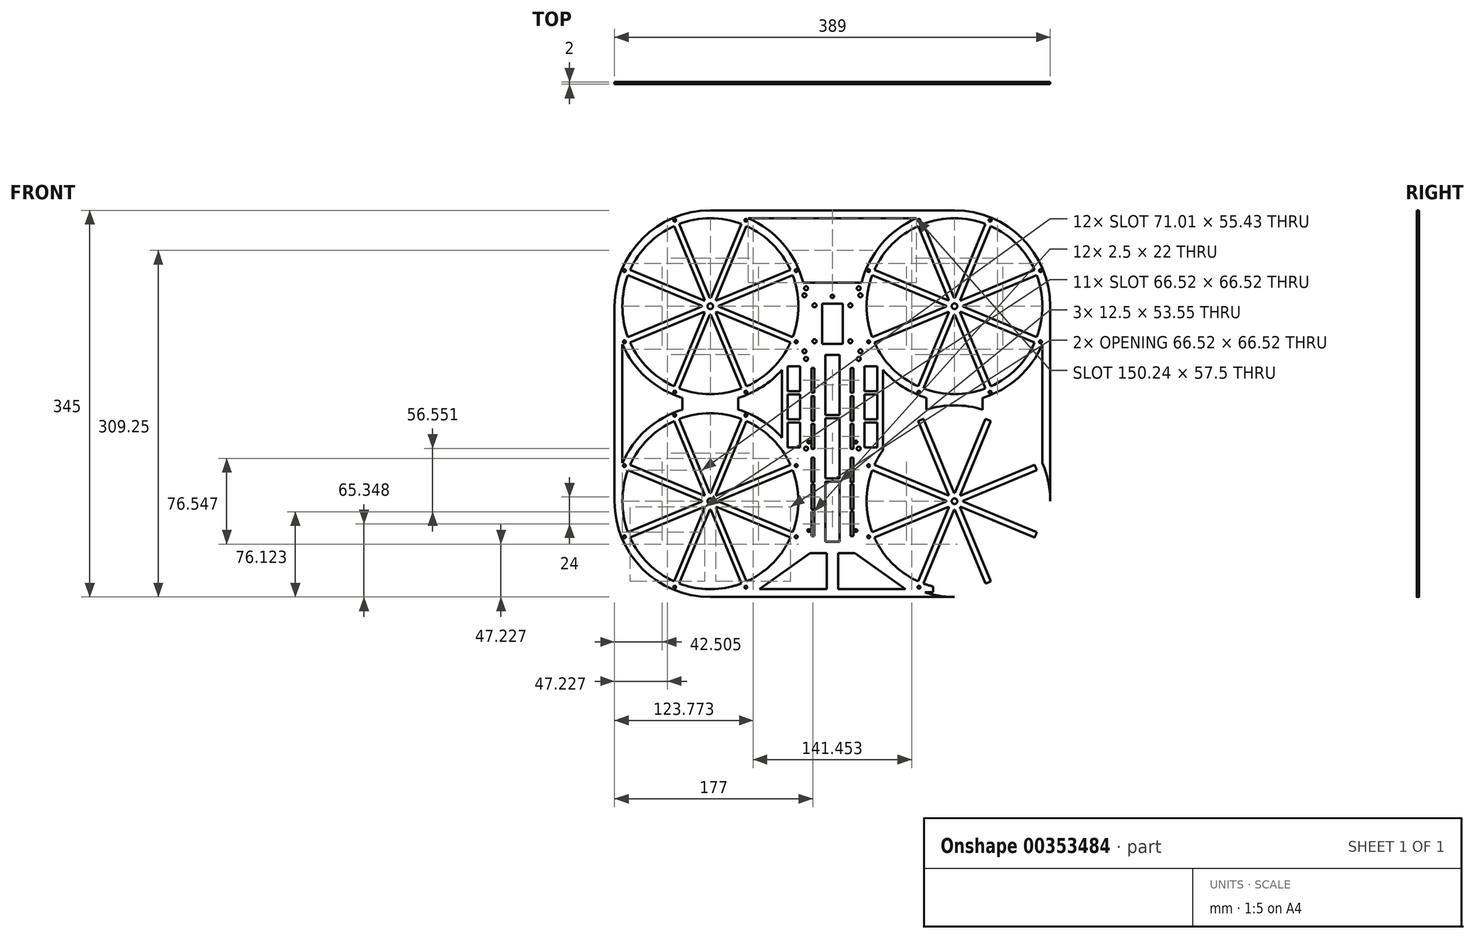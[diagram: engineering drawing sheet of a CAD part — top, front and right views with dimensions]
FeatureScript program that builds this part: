
annotation { "Feature Type Name" : "Feature", "Feature Type Description" : "" }
export const myFeature = defineFeature(function(context is Context, id is Id, definition is map)
    precondition{}
    {
        {
            var Q0;
            Q0=qCreatedBy(makeId("Front.planeOp"),FACE);
            var sketch = newSketch(context, id + "F0", { "sketchPlane" : qUnion([Q0])});
            skLineSegment(sketch, "E0", {"start": v(-45, -241.15) * mm, "end": v(-45, 0) * mm, "construction": true});
            skLineSegment(sketch, "E1", {"start": v(-45, 0) * mm, "end": v(45, 0) * mm});
            skLineSegment(sketch, "E2", {"start": v(45, 0) * mm, "end": v(45, -241.15) * mm, "construction": true});
            skLineSegment(sketch, "E3", {"start": v(5, -241.15) * mm, "end": v(5, -273.5) * mm, "construction": true});
            skLineSegment(sketch, "E4", {"start": v(-5, -273.5) * mm, "end": v(-5, -241.15) * mm, "construction": true});
            skLineSegment(sketch, "E5", {"start": v(-90, -271.29) * mm, "end": v(-90, -276.29) * mm});
            skLineSegment(sketch, "E6", {"start": v(-90, -276.29) * mm, "end": v(90, -276.29) * mm});
            skLineSegment(sketch, "E7", {"start": v(90, -276.29) * mm, "end": v(90, -271.29) * mm});
            skLineSegment(sketch, "E8", {"start": v(45, 0) * mm, "end": v(45, -241.15) * mm});
            skLineSegment(sketch, "E9", {"start": v(-45, 0) * mm, "end": v(-45, -241.15) * mm});
            skLineSegment(sketch, "E10", {"start": v(5, -241.15) * mm, "end": v(5, -273.5) * mm});
            skLineSegment(sketch, "E11", {"start": v(-5, -241.15) * mm, "end": v(-5, -273.5) * mm});
            skCircle(sketch, "E12", {"center": v(21, -221.15) * mm, "radius": 1.25 * mm});
            skCircle(sketch, "E13", {"center": v(21, -142.15) * mm, "radius": 1.25 * mm});
            skLineSegment(sketch, "E14", {"start": v(21, -221.15) * mm, "end": v(21, -142.15) * mm, "construction": true});
            skCircle(sketch, "E15.MirrorC", {"center": v(-21, -142.15) * mm, "radius": 1.25 * mm});
            skCircle(sketch, "E16.MirrorC", {"center": v(-21, -221.15) * mm, "radius": 1.25 * mm});
            skLineSegment(sketch, "E17", {"start": v(-21, -142.15) * mm, "end": v(21, -142.15) * mm});
            skLineSegment(sketch, "E18", {"start": v(-21, -221.15) * mm, "end": v(21, -221.15) * mm});
            skLineSegment(sketch, "E19", {"start": v(-20, -241.15) * mm, "end": v(-5, -241.15) * mm});
            skLineSegment(sketch, "E20", {"start": v(5, -241.15) * mm, "end": v(20, -241.15) * mm});
            skLineSegment(sketch, "E21", {"start": v(-65, -273.5) * mm, "end": v(-5, -273.5) * mm});
            skLineSegment(sketch, "E22", {"start": v(5, -273.5) * mm, "end": v(65, -273.5) * mm});
            skCircle(sketch, "E23", {"center": v(-23.5, -148) * mm, "radius": 1.75 * mm});
            skLineSegment(sketch, "E24", {"start": v(-23.5, -148) * mm, "end": v(-23.5, -5) * mm, "construction": true});
            skLineSegment(sketch, "E25", {"start": v(-23.5, -5) * mm, "end": v(23.5, -5) * mm, "construction": true});
            skCircle(sketch, "E26", {"center": v(-23.5, -5) * mm, "radius": 1.75 * mm});
            skCircle(sketch, "E27", {"center": v(-23.5, -68) * mm, "radius": 1.75 * mm});
            skCircle(sketch, "E28.MirrorC", {"center": v(23.5, -5) * mm, "radius": 1.75 * mm});
            skCircle(sketch, "E29.MirrorC", {"center": v(23.5, -68) * mm, "radius": 1.75 * mm});
            skCircle(sketch, "E30.MirrorC", {"center": v(23.5, -148) * mm, "radius": 1.75 * mm});
            skLineSegment(sketch, "E31.bottom", {"start": v(-108.5, -21) * mm, "end": v(108.5, -21) * mm, "construction": true});
            skLineSegment(sketch, "E31.top", {"start": v(-108.5, -195) * mm, "end": v(108.5, -195) * mm, "construction": true});
            skLineSegment(sketch, "E31.left", {"start": v(-108.5, -21) * mm, "end": v(-108.5, -195) * mm, "construction": true});
            skLineSegment(sketch, "E31.right", {"start": v(108.5, -21) * mm, "end": v(108.5, -195) * mm, "construction": true});
            skCircle(sketch, "E32", {"center": v(-108.5, -21) * mm, "radius": 78.5 * mm, "construction": true});
            skCircle(sketch, "E33", {"center": v(-108.5, -195) * mm, "radius": 78.5 * mm, "construction": true});
            skLineSegment(sketch, "E34", {"start": v(-20, -241.15) * mm, "end": v(-65, -273.5) * mm});
            skLineSegment(sketch, "E35", {"start": v(20, -241.15) * mm, "end": v(65, -273.5) * mm});
            skLineSegment(sketch, "E36", {"start": v(-45, -241.15) * mm, "end": v(-90, -271.29) * mm});
            skLineSegment(sketch, "E37", {"start": v(45, -241.15) * mm, "end": v(90, -271.29) * mm});
            skSolve(sketch);
        }
        {
            var Q0;
            Q0 = qSketchRegion(id + "F0", true);
            var Q1;
            {var subQ0=sQuery(id+"F0.wireOp",EDGE,"kQ9V0P2R-odBh-0fbW-jLHG-dfZg1nlExtGw");Q1=makeQuery(id+"F0.imprint","IMPRINT",FACE,{"disambiguationData":[TD([[makeQuery(id+"F0.imprint","IMPRINT",EDGE,{"derivedFrom":subQ0}),1.0]])]});}
            var Q2;
            {var subQ0=sQuery(id+"F0.wireOp",EDGE,"laIMQzsn-eaY8-GkRH-EcXH-4FRcY363x80o");Q2=makeQuery(id+"F0.imprint","IMPRINT",FACE,{"disambiguationData":[TD([[makeQuery(id+"F0.imprint","IMPRINT",EDGE,{"derivedFrom":subQ0}),-1.0]])]});}
            extrude(context, id + "F1", {"entities" : qUnion([Q0, Q1, Q2]), "offsetDistance" : 25 * mm, "depth" : 2 * mm});
        }
        {
            var Q0;
            Q0=makeQuery(id+"F1.opExtrude","CAP_FACE",FACE,{"disambiguationData":[OSD([sQuery(id+"F0.wireOp",EDGE,"E1"),sQuery(id+"F0.wireOp",EDGE,"E5"),sQuery(id+"F0.wireOp",EDGE,"E6"),sQuery(id+"F0.wireOp",EDGE,"E7"),sQuery(id+"F0.wireOp",EDGE,"E8"),sQuery(id+"F0.wireOp",EDGE,"E9"),sQuery(id+"F0.wireOp",EDGE,"E10"),sQuery(id+"F0.wireOp",EDGE,"E11"),sQuery(id+"F0.wireOp",EDGE,"E12"),sQuery(id+"F0.wireOp",EDGE,"E13"),sQuery(id+"F0.wireOp",EDGE,"E15.MirrorC"),sQuery(id+"F0.wireOp",EDGE,"E16.MirrorC"),sQuery(id+"F0.wireOp",EDGE,"zSTIlZa9-Mq1S-ZDe6-0sfO-W4MshlmDUBfW"),sQuery(id+"F0.wireOp",EDGE,"f6MW2Cg1-CikI-ga4A-lBPH-CLR3HkkBFIXh"),sQuery(id+"F0.wireOp",EDGE,"kKZFOv5i-oTwk-hDfM-zO1L-UuxxMlOX5rbl"),sQuery(id+"F0.wireOp",EDGE,"E19"),sQuery(id+"F0.wireOp",EDGE,"E20"),sQuery(id+"F0.wireOp",EDGE,"xO7viZK4-cgUC-NwoS-h9VV-xVzhR5ju8UwD"),sQuery(id+"F0.wireOp",EDGE,"9yqSDyW4-68Jc-LwH6-pWp7-TDNYJFoeOr4c"),sQuery(id+"F0.wireOp",EDGE,"E21"),sQuery(id+"F0.wireOp",EDGE,"E22"),sQuery(id+"F0.wireOp",EDGE,"pjrDvot8-T0ec-Pg6X-LkKo-KdkXjCvTm1g7"),sQuery(id+"F0.wireOp",EDGE,"E27"),sQuery(id+"F0.wireOp",EDGE,"E26"),sQuery(id+"F0.wireOp",EDGE,"E23"),sQuery(id+"F0.wireOp",EDGE,"E28.MirrorC"),sQuery(id+"F0.wireOp",EDGE,"E29.MirrorC"),sQuery(id+"F0.wireOp",EDGE,"E30.MirrorC"),sQuery(id+"F0.wireOp",EDGE,"6ebM2wVS-usP3-dKcT-XCbS-uj4wceOAEASt"),sQuery(id+"F0.wireOp",EDGE,"DVKAaTnB-kupf-vHmJ-fFrQ-rCFSXDP9MDJ3"),sQuery(id+"F0.wireOp",EDGE,"ROZdGaIm-NAGT-RCMa-KwZE-6l2WkTAMRBSw"),sQuery(id+"F0.wireOp",EDGE,"KL1P7Ti3-s2wI-81Sg-b8aw-ZE9qtUD7GHlb"),sQuery(id+"F0.wireOp",EDGE,"4kzRNWXD-2blB-KAq6-mfhZ-RD1CBBT0MYrh"),sQuery(id+"F0.wireOp",EDGE,"kIW8MdST-1OlK-D9hB-JnCF-jEkgTQVhUQcU"),sQuery(id+"F0.wireOp",EDGE,"r3YkkV02-pVVq-A2jz-rsv9-r8poLlV2KnUy"),sQuery(id+"F0.wireOp",EDGE,"ndt6MnIN-VhPU-kZhu-FrSA-9Hc000Z1pvMu"),sQuery(id+"F0.wireOp",EDGE,"kQ9V0P2R-odBh-0fbW-jLHG-dfZg1nlExtGw"),sQuery(id+"F0.wireOp",EDGE,"Powg7S7J-LFn7-6n4N-oK7u-LEDXEPLRkYPl"),sQuery(id+"F0.wireOp",EDGE,"laIMQzsn-eaY8-GkRH-EcXH-4FRcY363x80o"),sQuery(id+"F0.wireOp",EDGE,"faN3bw6d-osQ8-oTa0-kMRC-kvDlMTcLNJuj")])],"isStart":false});
            var sketch = newSketch(context, id + "F2", { "sketchPlane" : qUnion([Q0])});
            skLineSegment(sketch, "E38.bottom", {"start": v(-25, -11.25) * mm, "end": v(25, -11.25) * mm, "construction": true});
            skLineSegment(sketch, "E38.top", {"start": v(-25, -61.25) * mm, "end": v(25, -61.25) * mm, "construction": true});
            skLineSegment(sketch, "E38.left", {"start": v(-25, -11.25) * mm, "end": v(-25, -61.25) * mm, "construction": true});
            skLineSegment(sketch, "E38.right", {"start": v(25, -11.25) * mm, "end": v(25, -61.25) * mm, "construction": true});
            skCircle(sketch, "E39", {"center": v(-25, -11.25) * mm, "radius": 1.75 * mm});
            skCircle(sketch, "E40", {"center": v(25, -11.25) * mm, "radius": 1.75 * mm});
            skCircle(sketch, "E41", {"center": v(25, -61.25) * mm, "radius": 1.75 * mm});
            skCircle(sketch, "E42", {"center": v(-25, -61.25) * mm, "radius": 1.75 * mm});
            skLineSegment(sketch, "E43.bottom", {"start": v(-17.5, -66.25) * mm, "end": v(17.5, -66.25) * mm, "construction": true});
            skLineSegment(sketch, "E43.top", {"start": v(-17.5, -176.25) * mm, "end": v(17.5, -176.25) * mm, "construction": true});
            skLineSegment(sketch, "E43.left", {"start": v(-17.5, -66.25) * mm, "end": v(-17.5, -176.25) * mm, "construction": true});
            skLineSegment(sketch, "E43.right", {"start": v(17.5, -66.25) * mm, "end": v(17.5, -176.25) * mm, "construction": true});
            skLineSegment(sketch, "E44.bottom", {"start": v(-18.75, -180.15) * mm, "end": v(-16.25, -180.15) * mm});
            skLineSegment(sketch, "E44.top", {"start": v(-18.75, -202.15) * mm, "end": v(-16.25, -202.15) * mm});
            skLineSegment(sketch, "E44.left", {"start": v(-18.75, -180.15) * mm, "end": v(-18.75, -202.15) * mm});
            skLineSegment(sketch, "E44.right", {"start": v(-16.25, -180.15) * mm, "end": v(-16.25, -202.15) * mm});
            skLineSegment(sketch, "E45.bottom", {"start": v(-18.75, -126.15) * mm, "end": v(-16.25, -126.15) * mm});
            skLineSegment(sketch, "E45.top", {"start": v(-18.75, -148.15) * mm, "end": v(-16.25, -148.15) * mm});
            skLineSegment(sketch, "E45.left", {"start": v(-18.75, -126.15) * mm, "end": v(-18.75, -148.15) * mm});
            skLineSegment(sketch, "E45.right", {"start": v(-16.25, -126.15) * mm, "end": v(-16.25, -148.15) * mm});
            skLineSegment(sketch, "E46.bottom", {"start": v(-18.75, -204.15) * mm, "end": v(-16.25, -204.15) * mm});
            skLineSegment(sketch, "E46.top", {"start": v(-18.75, -226.15) * mm, "end": v(-16.25, -226.15) * mm});
            skLineSegment(sketch, "E46.left", {"start": v(-18.75, -204.15) * mm, "end": v(-18.75, -226.15) * mm});
            skLineSegment(sketch, "E46.right", {"start": v(-16.25, -204.15) * mm, "end": v(-16.25, -226.15) * mm});
            skLineSegment(sketch, "E47.bottom", {"start": v(-18.75, -156.15) * mm, "end": v(-16.25, -156.15) * mm});
            skLineSegment(sketch, "E47.top", {"start": v(-18.75, -178.15) * mm, "end": v(-16.25, -178.15) * mm});
            skLineSegment(sketch, "E47.left", {"start": v(-18.75, -156.15) * mm, "end": v(-18.75, -178.15) * mm});
            skLineSegment(sketch, "E47.right", {"start": v(-16.25, -156.15) * mm, "end": v(-16.25, -178.15) * mm});
            skLineSegment(sketch, "E48.MirrorCS", {"start": v(18.75, -180.15) * mm, "end": v(16.25, -180.15) * mm});
            skLineSegment(sketch, "E49.MirrorCS", {"start": v(17.5, -66.25) * mm, "end": v(-17.5, -66.25) * mm, "construction": true});
            skLineSegment(sketch, "E50.MirrorCS", {"start": v(18.75, -126.15) * mm, "end": v(16.25, -126.15) * mm});
            skLineSegment(sketch, "E51.MirrorCS", {"start": v(18.75, -148.15) * mm, "end": v(16.25, -148.15) * mm});
            skLineSegment(sketch, "E52.MirrorCS", {"start": v(18.75, -202.15) * mm, "end": v(16.25, -202.15) * mm});
            skLineSegment(sketch, "E53.MirrorCS", {"start": v(18.75, -204.15) * mm, "end": v(16.25, -204.15) * mm});
            skLineSegment(sketch, "E54.MirrorCS", {"start": v(18.75, -156.15) * mm, "end": v(16.25, -156.15) * mm});
            skLineSegment(sketch, "E55.MirrorCS", {"start": v(18.75, -226.15) * mm, "end": v(16.25, -226.15) * mm});
            skLineSegment(sketch, "E56.MirrorCS", {"start": v(18.75, -178.15) * mm, "end": v(16.25, -178.15) * mm});
            skLineSegment(sketch, "E57.MirrorCS", {"start": v(18.75, -204.15) * mm, "end": v(18.75, -226.15) * mm});
            skLineSegment(sketch, "E58.MirrorCS", {"start": v(18.75, -126.15) * mm, "end": v(18.75, -148.15) * mm});
            skLineSegment(sketch, "E59.MirrorCS", {"start": v(16.25, -126.15) * mm, "end": v(16.25, -148.15) * mm});
            skLineSegment(sketch, "E60.MirrorCS", {"start": v(18.75, -156.15) * mm, "end": v(18.75, -178.15) * mm});
            skLineSegment(sketch, "E61.MirrorCS", {"start": v(16.25, -204.15) * mm, "end": v(16.25, -226.15) * mm});
            skLineSegment(sketch, "E62.MirrorCS", {"start": v(16.25, -180.15) * mm, "end": v(16.25, -202.15) * mm});
            skLineSegment(sketch, "E63.MirrorCS", {"start": v(18.75, -180.15) * mm, "end": v(18.75, -202.15) * mm});
            skLineSegment(sketch, "E64.MirrorCS", {"start": v(16.25, -156.15) * mm, "end": v(16.25, -178.15) * mm});
            skCircle(sketch, "E65", {"center": v(-25, -11.25) * mm, "radius": 2.75 * mm, "construction": true});
            skCircle(sketch, "E66", {"center": v(-23.5, -5) * mm, "radius": 2.75 * mm, "construction": true});
            skLineSegment(sketch, "E67.bottom", {"start": v(-16, -20.25) * mm, "end": v(16, -20.25) * mm, "construction": true});
            skLineSegment(sketch, "E67.top", {"start": v(-16, -52.25) * mm, "end": v(16, -52.25) * mm, "construction": true});
            skLineSegment(sketch, "E67.left", {"start": v(-16, -20.25) * mm, "end": v(-16, -52.25) * mm, "construction": true});
            skLineSegment(sketch, "E67.right", {"start": v(16, -20.25) * mm, "end": v(16, -52.25) * mm, "construction": true});
            skCircle(sketch, "E68", {"center": v(16, -20.25) * mm, "radius": 1.75 * mm});
            skCircle(sketch, "E69", {"center": v(16, -52.25) * mm, "radius": 1.75 * mm});
            skCircle(sketch, "E70", {"center": v(-16, -52.25) * mm, "radius": 1.75 * mm});
            skCircle(sketch, "E71", {"center": v(-16, -20.25) * mm, "radius": 1.75 * mm});
            skLineSegment(sketch, "E72.0.1.0", {"start": v(16.25, -101.15) * mm, "end": v(16.25, -123.15) * mm});
            skLineSegment(sketch, "E72.0.1.1", {"start": v(-18.75, -101.15) * mm, "end": v(-18.75, -123.15) * mm});
            skLineSegment(sketch, "E72.0.1.2", {"start": v(-16.25, -101.15) * mm, "end": v(-16.25, -123.15) * mm});
            skLineSegment(sketch, "E72.0.1.3", {"start": v(18.75, -101.15) * mm, "end": v(18.75, -123.15) * mm});
            skLineSegment(sketch, "E72.0.1.4", {"start": v(-18.75, -123.15) * mm, "end": v(-16.25, -123.15) * mm});
            skLineSegment(sketch, "E72.0.1.5", {"start": v(18.75, -123.15) * mm, "end": v(16.25, -123.15) * mm});
            skLineSegment(sketch, "E72.0.1.6", {"start": v(-18.75, -101.15) * mm, "end": v(-16.25, -101.15) * mm});
            skLineSegment(sketch, "E72.0.1.7", {"start": v(18.75, -101.15) * mm, "end": v(16.25, -101.15) * mm});
            skLineSegment(sketch, "E72.0.2.0", {"start": v(16.25, -76.15) * mm, "end": v(16.25, -98.15) * mm});
            skLineSegment(sketch, "E72.0.2.1", {"start": v(-18.75, -76.15) * mm, "end": v(-18.75, -98.15) * mm});
            skLineSegment(sketch, "E72.0.2.2", {"start": v(-16.25, -76.15) * mm, "end": v(-16.25, -98.15) * mm});
            skLineSegment(sketch, "E72.0.2.3", {"start": v(18.75, -76.15) * mm, "end": v(18.75, -98.15) * mm});
            skLineSegment(sketch, "E72.0.2.4", {"start": v(-18.75, -98.15) * mm, "end": v(-16.25, -98.15) * mm});
            skLineSegment(sketch, "E72.0.2.5", {"start": v(18.75, -98.15) * mm, "end": v(16.25, -98.15) * mm});
            skLineSegment(sketch, "E72.0.2.6", {"start": v(-18.75, -76.15) * mm, "end": v(-16.25, -76.15) * mm});
            skLineSegment(sketch, "E72.0.2.7", {"start": v(18.75, -76.15) * mm, "end": v(16.25, -76.15) * mm});
            skLineSegment(sketch, "E72.direction1", {"start": v(-18.75, -148.15) * mm, "end": v(6.25, -148.15) * mm, "construction": true});
            skLineSegment(sketch, "E72.direction2", {"start": v(-18.75, -148.15) * mm, "end": v(-18.75, -123.15) * mm, "construction": true});
            skSolve(sketch);
        }
        {
            var Q0;
            Q0 = qSketchRegion(id + "F2", true);
            extrude(context, id + "F3", {"entities" : qUnion([Q0]), "operationType" : NewBodyOperationType.REMOVE, "endBound" : BoundingType.THROUGH_ALL, "oppositeDirection" : true, "depth" : 25 * mm, "offsetDistance" : 25 * mm});
        }
        {
            var Q0;
            Q0=makeQuery(id+"F1.opExtrude","CAP_FACE",FACE,{"disambiguationData":[OSD([sQuery(id+"F0.wireOp",EDGE,"E1"),sQuery(id+"F0.wireOp",EDGE,"E5"),sQuery(id+"F0.wireOp",EDGE,"E6"),sQuery(id+"F0.wireOp",EDGE,"E7"),sQuery(id+"F0.wireOp",EDGE,"E8"),sQuery(id+"F0.wireOp",EDGE,"E9"),sQuery(id+"F0.wireOp",EDGE,"E10"),sQuery(id+"F0.wireOp",EDGE,"E11"),sQuery(id+"F0.wireOp",EDGE,"E12"),sQuery(id+"F0.wireOp",EDGE,"E13"),sQuery(id+"F0.wireOp",EDGE,"E15.MirrorC"),sQuery(id+"F0.wireOp",EDGE,"E16.MirrorC"),sQuery(id+"F0.wireOp",EDGE,"zSTIlZa9-Mq1S-ZDe6-0sfO-W4MshlmDUBfW"),sQuery(id+"F0.wireOp",EDGE,"f6MW2Cg1-CikI-ga4A-lBPH-CLR3HkkBFIXh"),sQuery(id+"F0.wireOp",EDGE,"kKZFOv5i-oTwk-hDfM-zO1L-UuxxMlOX5rbl"),sQuery(id+"F0.wireOp",EDGE,"E19"),sQuery(id+"F0.wireOp",EDGE,"E20"),sQuery(id+"F0.wireOp",EDGE,"xO7viZK4-cgUC-NwoS-h9VV-xVzhR5ju8UwD"),sQuery(id+"F0.wireOp",EDGE,"9yqSDyW4-68Jc-LwH6-pWp7-TDNYJFoeOr4c"),sQuery(id+"F0.wireOp",EDGE,"E21"),sQuery(id+"F0.wireOp",EDGE,"E22"),sQuery(id+"F0.wireOp",EDGE,"pjrDvot8-T0ec-Pg6X-LkKo-KdkXjCvTm1g7"),sQuery(id+"F0.wireOp",EDGE,"E27"),sQuery(id+"F0.wireOp",EDGE,"E26"),sQuery(id+"F0.wireOp",EDGE,"E23"),sQuery(id+"F0.wireOp",EDGE,"E28.MirrorC"),sQuery(id+"F0.wireOp",EDGE,"E29.MirrorC"),sQuery(id+"F0.wireOp",EDGE,"E30.MirrorC")])],"isStart":false});
            var sketch = newSketch(context, id + "F4", { "sketchPlane" : qUnion([Q0])});
            skLineSegment(sketch, "E73.bottom", {"start": v(-109, -21) * mm, "end": v(109, -21) * mm, "construction": true});
            skLineSegment(sketch, "E73.top", {"start": v(-109, -195) * mm, "end": v(109, -195) * mm, "construction": true});
            skLineSegment(sketch, "E73.left", {"start": v(-109, -21) * mm, "end": v(-109, -195) * mm, "construction": true});
            skLineSegment(sketch, "E73.right", {"start": v(109, -21) * mm, "end": v(109, -195) * mm, "construction": true});
            skCircle(sketch, "E74", {"center": v(-109, -21) * mm, "radius": 78.5 * mm, "construction": true});
            skCircle(sketch, "E75", {"center": v(109, -21) * mm, "radius": 78.5 * mm, "construction": true});
            skLineSegment(sketch, "E76", {"start": v(-33.36, 0) * mm, "end": v(-45, 0) * mm});
            skLineSegment(sketch, "E77", {"start": v(-45, 0) * mm, "end": v(-45, -66.46) * mm});
            skLineSegment(sketch, "E78", {"start": v(33.36, 0) * mm, "end": v(45, 0) * mm});
            skLineSegment(sketch, "E79", {"start": v(45, 0) * mm, "end": v(45, -66.46) * mm});
            skArc(sketch, "E80", {"start": v(-33.36, 0) * mm, "mid": v(-31.68, -34.54) * mm, "end": v(-45, -66.46) * mm});
            skArc(sketch, "E81", {"start": v(33.36, 0) * mm, "mid": v(31.68, -34.54) * mm, "end": v(45, -66.46) * mm});
            skCircle(sketch, "E82", {"center": v(-109, -21) * mm, "radius": 85.5 * mm, "construction": true});
            skCircle(sketch, "E83", {"center": v(109, -195) * mm, "radius": 78.5 * mm, "construction": true});
            skCircle(sketch, "E84", {"center": v(109, -195) * mm, "radius": 85.5 * mm, "construction": true});
            skCircle(sketch, "E85", {"center": v(-109, -195) * mm, "radius": 78.5 * mm, "construction": true});
            skCircle(sketch, "E86", {"center": v(-109, -195) * mm, "radius": 85.5 * mm, "construction": true});
            skCircle(sketch, "E87", {"center": v(109, -21) * mm, "radius": 85.5 * mm, "construction": true});
            skCircle(sketch, "E88.cCircle", {"center": v(109, -195) * mm, "radius": 83 * mm, "construction": true});
            skLineSegment(sketch, "E88.0", {"start": v(140.76, -118.32) * mm, "end": v(185.68, -163.24) * mm, "construction": true});
            skLineSegment(sketch, "E88.1", {"start": v(185.68, -163.24) * mm, "end": v(185.68, -226.76) * mm, "construction": true});
            skLineSegment(sketch, "E88.2", {"start": v(185.68, -226.76) * mm, "end": v(140.76, -271.68) * mm, "construction": true});
            skLineSegment(sketch, "E88.3", {"start": v(140.76, -271.68) * mm, "end": v(77.24, -271.68) * mm, "construction": true});
            skLineSegment(sketch, "E88.4", {"start": v(77.24, -271.68) * mm, "end": v(32.32, -226.76) * mm, "construction": true});
            skLineSegment(sketch, "E88.5", {"start": v(32.32, -226.76) * mm, "end": v(32.32, -163.24) * mm, "construction": true});
            skLineSegment(sketch, "E88.6", {"start": v(32.32, -163.24) * mm, "end": v(77.24, -118.32) * mm, "construction": true});
            skLineSegment(sketch, "E88.7", {"start": v(77.24, -118.32) * mm, "end": v(140.76, -118.32) * mm, "construction": true});
            skCircle(sketch, "E89.cCircle", {"center": v(-109, -21) * mm, "radius": 83 * mm, "construction": true});
            skLineSegment(sketch, "E89.0", {"start": v(-185.68, 10.76) * mm, "end": v(-140.76, 55.68) * mm, "construction": true});
            skLineSegment(sketch, "E89.1", {"start": v(-140.76, 55.68) * mm, "end": v(-77.24, 55.68) * mm, "construction": true});
            skLineSegment(sketch, "E89.2", {"start": v(-77.24, 55.68) * mm, "end": v(-32.32, 10.76) * mm, "construction": true});
            skLineSegment(sketch, "E89.3", {"start": v(-32.32, 10.76) * mm, "end": v(-32.32, -52.76) * mm, "construction": true});
            skLineSegment(sketch, "E89.4", {"start": v(-32.32, -52.76) * mm, "end": v(-77.24, -97.68) * mm, "construction": true});
            skLineSegment(sketch, "E89.5", {"start": v(-77.24, -97.68) * mm, "end": v(-140.76, -97.68) * mm, "construction": true});
            skLineSegment(sketch, "E89.6", {"start": v(-140.76, -97.68) * mm, "end": v(-185.68, -52.76) * mm, "construction": true});
            skLineSegment(sketch, "E89.7", {"start": v(-185.68, -52.76) * mm, "end": v(-185.68, 10.76) * mm, "construction": true});
            skCircle(sketch, "E90.cCircle", {"center": v(109, -21) * mm, "radius": 83 * mm, "construction": true});
            skLineSegment(sketch, "E90.0", {"start": v(140.76, 55.68) * mm, "end": v(185.68, 10.76) * mm, "construction": true});
            skLineSegment(sketch, "E90.1", {"start": v(185.68, 10.76) * mm, "end": v(185.68, -52.76) * mm, "construction": true});
            skLineSegment(sketch, "E90.2", {"start": v(185.68, -52.76) * mm, "end": v(140.76, -97.68) * mm, "construction": true});
            skLineSegment(sketch, "E90.3", {"start": v(140.76, -97.68) * mm, "end": v(77.24, -97.68) * mm, "construction": true});
            skLineSegment(sketch, "E90.4", {"start": v(77.24, -97.68) * mm, "end": v(32.32, -52.76) * mm, "construction": true});
            skLineSegment(sketch, "E90.5", {"start": v(32.32, -52.76) * mm, "end": v(32.32, 10.76) * mm, "construction": true});
            skLineSegment(sketch, "E90.6", {"start": v(32.32, 10.76) * mm, "end": v(77.24, 55.68) * mm, "construction": true});
            skLineSegment(sketch, "E90.7", {"start": v(77.24, 55.68) * mm, "end": v(140.76, 55.68) * mm, "construction": true});
            skCircle(sketch, "E91.cCircle", {"center": v(-109, -195) * mm, "radius": 83 * mm, "construction": true});
            skLineSegment(sketch, "E91.0", {"start": v(-140.76, -118.32) * mm, "end": v(-77.24, -118.32) * mm, "construction": true});
            skLineSegment(sketch, "E91.1", {"start": v(-77.24, -118.32) * mm, "end": v(-32.32, -163.24) * mm, "construction": true});
            skLineSegment(sketch, "E91.2", {"start": v(-32.32, -163.24) * mm, "end": v(-32.32, -226.76) * mm, "construction": true});
            skLineSegment(sketch, "E91.3", {"start": v(-32.32, -226.76) * mm, "end": v(-77.24, -271.68) * mm, "construction": true});
            skLineSegment(sketch, "E91.4", {"start": v(-77.24, -271.68) * mm, "end": v(-140.76, -271.68) * mm, "construction": true});
            skLineSegment(sketch, "E91.5", {"start": v(-140.76, -271.68) * mm, "end": v(-185.68, -226.76) * mm, "construction": true});
            skLineSegment(sketch, "E91.6", {"start": v(-185.68, -226.76) * mm, "end": v(-185.68, -163.24) * mm, "construction": true});
            skLineSegment(sketch, "E91.7", {"start": v(-185.68, -163.24) * mm, "end": v(-140.76, -118.32) * mm, "construction": true});
            skCircle(sketch, "E92", {"center": v(-32.32, -52.76) * mm, "radius": 1.25 * mm});
            skCircle(sketch, "E93", {"center": v(-32.32, -163.24) * mm, "radius": 1.25 * mm});
            skCircle(sketch, "E94", {"center": v(32.32, -163.24) * mm, "radius": 1.25 * mm});
            skCircle(sketch, "E95", {"center": v(32.32, -52.76) * mm, "radius": 1.25 * mm});
            skCircle(sketch, "E96", {"center": v(-140.76, -118.32) * mm, "radius": 1.25 * mm, "construction": true});
            skCircle(sketch, "E97", {"center": v(-25, -11.25) * mm, "radius": 3 * mm, "construction": true});
            skCircle(sketch, "E98", {"center": v(-23.5, -5) * mm, "radius": 3 * mm, "construction": true});
            skLineSegment(sketch, "E99", {"start": v(-26.12, 0) * mm, "end": v(-28.5, 0) * mm, "construction": true});
            skLineSegment(sketch, "E100", {"start": v(-28.5, 0) * mm, "end": v(-28.5, -42) * mm, "construction": true});
            skLineSegment(sketch, "E101", {"start": v(-28.5, -42) * mm, "end": v(-26.12, -42) * mm, "construction": true});
            skLineSegment(sketch, "E102", {"start": v(-109, -116.5) * mm, "end": v(-190.8, -116.5) * mm, "construction": true});
            skLineSegment(sketch, "E103", {"start": v(0, -195) * mm, "end": v(-32.32, -226.76) * mm, "construction": true});
            skLineSegment(sketch, "E104", {"start": v(32.32, -226.76) * mm, "end": v(-32.32, -226.76) * mm, "construction": true});
            skLineSegment(sketch, "E105", {"start": v(32.32, -226.76) * mm, "end": v(0, -195) * mm, "construction": true});
            skLineSegment(sketch, "E106", {"start": v(0, -203.76) * mm, "end": v(0, -226.76) * mm, "construction": true});
            skPoint(sketch, "E106.endSnap0", {"position": v(0, -226.76) * mm});
            skLineSegment(sketch, "E107", {"start": v(-32.32, 10.76) * mm, "end": v(32.32, 10.76) * mm, "construction": true});
            skLineSegment(sketch, "E108", {"start": v(32.32, 10.76) * mm, "end": v(0, -12.24) * mm, "construction": true});
            skLineSegment(sketch, "E109", {"start": v(0, -12.24) * mm, "end": v(-32.32, 10.76) * mm, "construction": true});
            skCircle(sketch, "E110", {"center": v(0, -203.76) * mm, "radius": 1.5 * mm});
            skCircle(sketch, "E111", {"center": v(0, -12.24) * mm, "radius": 1.5 * mm});
            skArc(sketch, "E112", {"start": v(-33.36, 0) * mm, "mid": v(-186.32, -7.46) * mm, "end": v(-45, -66.46) * mm});
            skArc(sketch, "E113", {"start": v(-26.12, 0) * mm, "mid": v(-192.08, -0.8) * mm, "end": v(-45, -77.7) * mm, "construction": true});
            skLineSegment(sketch, "E114", {"start": v(-33.36, 0) * mm, "end": v(-26.12, 0) * mm});
            skLineSegment(sketch, "E115", {"start": v(-45, -77.7) * mm, "end": v(-45, -66.46) * mm});
            skArc(sketch, "E116", {"start": v(-45, -77.7) * mm, "mid": v(-192.08, -0.8) * mm, "end": v(-26.12, 0) * mm});
            skArc(sketch, "E117", {"start": v(45, -66.46) * mm, "mid": v(186.32, -7.46) * mm, "end": v(33.36, 0) * mm});
            skArc(sketch, "E118", {"start": v(26.12, 0) * mm, "mid": v(192.08, -0.8) * mm, "end": v(45, -77.7) * mm});
            skArc(sketch, "E119", {"start": v(-45, -149.54) * mm, "mid": v(-35.38, -222.24) * mm, "end": v(-90, -271.17) * mm});
            skLineSegment(sketch, "E120", {"start": v(-45, -149.54) * mm, "end": v(-45, -241.15) * mm});
            skLineSegment(sketch, "E121", {"start": v(-45, -241.15) * mm, "end": v(-90, -271.29) * mm});
            skLineSegment(sketch, "E122", {"start": v(-90, -271.29) * mm, "end": v(-90, -271.29) * mm});
            skLineSegment(sketch, "E123", {"start": v(-90, -271.17) * mm, "end": v(-90, -271.29) * mm});
            skArc(sketch, "E124", {"start": v(-45, -138.3) * mm, "mid": v(-191.5, -172.58) * mm, "end": v(-82.5, -276.29) * mm});
            skArc(sketch, "E125", {"start": v(-45, -149.54) * mm, "mid": v(-182.62, -167.76) * mm, "end": v(-90, -271.17) * mm});
            skLineSegment(sketch, "E126.MirrorCS", {"start": v(45, -149.54) * mm, "end": v(45, -241.15) * mm});
            skLineSegment(sketch, "E127.MirrorCS", {"start": v(-32.32, -226.76) * mm, "end": v(32.32, -226.76) * mm, "construction": true});
            skLineSegment(sketch, "E128.MirrorCS", {"start": v(32.32, -226.76) * mm, "end": v(77.24, -271.68) * mm, "construction": true});
            skLineSegment(sketch, "E129.MirrorCS", {"start": v(32.32, -163.24) * mm, "end": v(32.32, -226.76) * mm, "construction": true});
            skArc(sketch, "E130", {"start": v(45, -149.54) * mm, "mid": v(35.38, -222.24) * mm, "end": v(90, -271.17) * mm});
            skLineSegment(sketch, "E131", {"start": v(90, -271.29) * mm, "end": v(90, -271.17) * mm});
            skLineSegment(sketch, "E132", {"start": v(90, -271.29) * mm, "end": v(45, -241.15) * mm});
            skArc(sketch, "E133", {"start": v(45, -138.3) * mm, "mid": v(191.5, -172.58) * mm, "end": v(82.5, -276.29) * mm});
            skArc(sketch, "E134", {"start": v(90, -271.17) * mm, "mid": v(182.62, -167.76) * mm, "end": v(45, -149.54) * mm});
            skSolve(sketch);
        }
        {
            var Q0;
            Q0 = qSketchRegion(id + "F4", true);
            extrude(context, id + "F5", {"entities" : qUnion([Q0]), "operationType" : NewBodyOperationType.REMOVE, "endBound" : BoundingType.THROUGH_ALL, "oppositeDirection" : true, "depth" : 25 * mm, "offsetDistance" : 25 * mm});
        }
        {
            var Q0;
            Q0=makeQuery(id+"FMxjOZTch3q8zvc_1.boolean.opBoolean","MERGE",FACE,{"derivedFrom":[makeQuery(id+"F1.opExtrude","CAP_FACE",FACE,{"disambiguationData":[OSD([sQuery(id+"F0.wireOp",EDGE,"E1"),sQuery(id+"F0.wireOp",EDGE,"E5"),sQuery(id+"F0.wireOp",EDGE,"E6"),sQuery(id+"F0.wireOp",EDGE,"E7"),sQuery(id+"F0.wireOp",EDGE,"E8"),sQuery(id+"F0.wireOp",EDGE,"E9"),sQuery(id+"F0.wireOp",EDGE,"E10"),sQuery(id+"F0.wireOp",EDGE,"E11"),sQuery(id+"F0.wireOp",EDGE,"E12"),sQuery(id+"F0.wireOp",EDGE,"E13"),sQuery(id+"F0.wireOp",EDGE,"E15.MirrorC"),sQuery(id+"F0.wireOp",EDGE,"E16.MirrorC"),sQuery(id+"F0.wireOp",EDGE,"zSTIlZa9-Mq1S-ZDe6-0sfO-W4MshlmDUBfW"),sQuery(id+"F0.wireOp",EDGE,"f6MW2Cg1-CikI-ga4A-lBPH-CLR3HkkBFIXh"),sQuery(id+"F0.wireOp",EDGE,"kKZFOv5i-oTwk-hDfM-zO1L-UuxxMlOX5rbl"),sQuery(id+"F0.wireOp",EDGE,"E19"),sQuery(id+"F0.wireOp",EDGE,"E20"),sQuery(id+"F0.wireOp",EDGE,"xO7viZK4-cgUC-NwoS-h9VV-xVzhR5ju8UwD"),sQuery(id+"F0.wireOp",EDGE,"9yqSDyW4-68Jc-LwH6-pWp7-TDNYJFoeOr4c"),sQuery(id+"F0.wireOp",EDGE,"E21"),sQuery(id+"F0.wireOp",EDGE,"E22"),sQuery(id+"F0.wireOp",EDGE,"pjrDvot8-T0ec-Pg6X-LkKo-KdkXjCvTm1g7"),sQuery(id+"F0.wireOp",EDGE,"E27"),sQuery(id+"F0.wireOp",EDGE,"E26"),sQuery(id+"F0.wireOp",EDGE,"E23"),sQuery(id+"F0.wireOp",EDGE,"E28.MirrorC"),sQuery(id+"F0.wireOp",EDGE,"E29.MirrorC"),sQuery(id+"F0.wireOp",EDGE,"E30.MirrorC")])],"isStart":false})],"fromTools":[makeQuery(id+"FMxjOZTch3q8zvc_1.opExtrude","SWEPT_FACE",FACE,{"disambiguationData":[OSD([sQuery(id+"FXnTs9Vk96qBHkO_1.wireOp",EDGE,"2qYHMhsn-Td8y-HjAB-3SRO-Tm7Y1iTeiUua.top")])]}),makeQuery(id+"FMxjOZTch3q8zvc_1.opExtrude","SWEPT_FACE",FACE,{"disambiguationData":[OSD([sQuery(id+"FXnTs9Vk96qBHkO_1.wireOp",EDGE,"225656be-2882-4732-a1c9-cd1c7ffdf3812.MirrorCS")])]})]});
            var sketch = newSketch(context, id + "F6", { "sketchPlane" : qUnion([Q0])});
            skLineSegment(sketch, "E135.bottom", {"start": v(-40, -74.75) * mm, "end": v(-28.75, -74.75) * mm});
            skLineSegment(sketch, "E135.top", {"start": v(-40, -96.83) * mm, "end": v(-28.75, -96.83) * mm});
            skLineSegment(sketch, "E135.left", {"start": v(-40, -74.75) * mm, "end": v(-40, -96.83) * mm});
            skLineSegment(sketch, "E135.right", {"start": v(-28.75, -74.75) * mm, "end": v(-28.75, -96.83) * mm});
            skLineSegment(sketch, "E136.bottom", {"start": v(28.75, -74.75) * mm, "end": v(40, -74.75) * mm});
            skLineSegment(sketch, "E136.top", {"start": v(28.75, -96.83) * mm, "end": v(40, -96.83) * mm});
            skLineSegment(sketch, "E136.left", {"start": v(28.75, -74.75) * mm, "end": v(28.75, -96.83) * mm});
            skLineSegment(sketch, "E136.right", {"start": v(40, -74.75) * mm, "end": v(40, -96.83) * mm});
            skLineSegment(sketch, "E137.bottom", {"start": v(-6.25, -64.5) * mm, "end": v(6.25, -64.5) * mm});
            skLineSegment(sketch, "E137.top", {"start": v(-6.25, -118.05) * mm, "end": v(6.25, -118.05) * mm});
            skLineSegment(sketch, "E137.left", {"start": v(-6.25, -64.5) * mm, "end": v(-6.25, -118.05) * mm});
            skLineSegment(sketch, "E137.right", {"start": v(6.25, -64.5) * mm, "end": v(6.25, -118.05) * mm});
            skLineSegment(sketch, "E138.bottom", {"start": v(-9.25, -18.74) * mm, "end": v(9.25, -18.74) * mm});
            skLineSegment(sketch, "E138.top", {"start": v(-9.25, -54.5) * mm, "end": v(9.25, -54.5) * mm});
            skLineSegment(sketch, "E138.left", {"start": v(-9.25, -18.74) * mm, "end": v(-9.25, -54.5) * mm});
            skLineSegment(sketch, "E138.right", {"start": v(9.25, -18.74) * mm, "end": v(9.25, -54.5) * mm});
            skLineSegment(sketch, "E139.bottom", {"start": v(-6.25, -177.6) * mm, "end": v(6.25, -177.6) * mm});
            skLineSegment(sketch, "E139.top", {"start": v(-6.25, -231.15) * mm, "end": v(6.25, -231.15) * mm});
            skLineSegment(sketch, "E139.left", {"start": v(-6.25, -177.6) * mm, "end": v(-6.25, -231.15) * mm});
            skLineSegment(sketch, "E139.right", {"start": v(6.25, -177.6) * mm, "end": v(6.25, -231.15) * mm});
            skLineSegment(sketch, "E140.bottom", {"start": v(-6.25, -121.05) * mm, "end": v(6.25, -121.05) * mm});
            skLineSegment(sketch, "E140.top", {"start": v(-6.25, -174.6) * mm, "end": v(6.25, -174.6) * mm});
            skLineSegment(sketch, "E140.left", {"start": v(-6.25, -121.05) * mm, "end": v(-6.25, -174.6) * mm});
            skLineSegment(sketch, "E140.right", {"start": v(6.25, -121.05) * mm, "end": v(6.25, -174.6) * mm});
            skLineSegment(sketch, "E141.bottom", {"start": v(28.75, -99.83) * mm, "end": v(40, -99.83) * mm});
            skLineSegment(sketch, "E141.top", {"start": v(28.75, -121.9) * mm, "end": v(40, -121.9) * mm});
            skLineSegment(sketch, "E141.left", {"start": v(28.75, -99.83) * mm, "end": v(28.75, -121.9) * mm});
            skLineSegment(sketch, "E141.right", {"start": v(40, -99.83) * mm, "end": v(40, -121.9) * mm});
            skLineSegment(sketch, "E142.bottom", {"start": v(28.75, -124.9) * mm, "end": v(40, -124.9) * mm});
            skLineSegment(sketch, "E142.top", {"start": v(28.75, -146.99) * mm, "end": v(40, -146.99) * mm});
            skLineSegment(sketch, "E142.left", {"start": v(28.75, -124.9) * mm, "end": v(28.75, -146.99) * mm});
            skLineSegment(sketch, "E142.right", {"start": v(40, -124.9) * mm, "end": v(40, -146.99) * mm});
            skLineSegment(sketch, "E143.bottom", {"start": v(-40, -99.83) * mm, "end": v(-28.75, -99.83) * mm});
            skLineSegment(sketch, "E143.top", {"start": v(-40, -121.9) * mm, "end": v(-28.75, -121.9) * mm});
            skLineSegment(sketch, "E143.left", {"start": v(-40, -99.83) * mm, "end": v(-40, -121.9) * mm});
            skLineSegment(sketch, "E143.right", {"start": v(-28.75, -99.83) * mm, "end": v(-28.75, -121.9) * mm});
            skLineSegment(sketch, "E144.bottom", {"start": v(-28.75, -124.9) * mm, "end": v(-40, -124.9) * mm});
            skLineSegment(sketch, "E144.top", {"start": v(-28.75, -146.99) * mm, "end": v(-40, -146.99) * mm});
            skLineSegment(sketch, "E144.left", {"start": v(-28.75, -124.9) * mm, "end": v(-28.75, -146.99) * mm});
            skLineSegment(sketch, "E144.right", {"start": v(-40, -124.9) * mm, "end": v(-40, -146.99) * mm});
            skSolve(sketch);
        }
        {
            var Q0;
            Q0 = qSketchRegion(id + "F6", true);
            extrude(context, id + "F7", {"entities" : qUnion([Q0]), "operationType" : NewBodyOperationType.REMOVE, "endBound" : BoundingType.THROUGH_ALL, "oppositeDirection" : true, "depth" : 25 * mm, "offsetDistance" : 25 * mm});
        }
        {
            var Q0;
            Q0=makeQuery(id+"F4.imprint","IMPRINT",FACE,{"disambiguationData":[TD([[makeQuery(id+"F4.imprint","IMPRINT",EDGE,{"derivedFrom":sQuery(id+"F4.wireOp",EDGE,"E112")}),-1.0]])]});
            var Q1;
            {var subQ0=sQuery(id+"F4.wireOp",EDGE,"E117");Q1=makeQuery(id+"F4.imprint","IMPRINT",FACE,{"disambiguationData":[TD([[makeQuery(id+"F4.imprint","IMPRINT",EDGE,{"derivedFrom":subQ0}),-1.0]])]});}
            var Q2;
            {var subQ5=sQuery(id+"F4.wireOp",EDGE,"E124");Q2=makeQuery(id+"F4.imprint","IMPRINT",FACE,{"disambiguationData":[TD([[makeQuery(id+"F4.imprint","IMPRINT",EDGE,{"derivedFrom":subQ5}),1.0]])]});}
            var Q3;
            {var subQ6=sQuery(id+"F4.wireOp",EDGE,"E133");Q3=makeQuery(id+"F4.imprint","IMPRINT",FACE,{"disambiguationData":[TD([[makeQuery(id+"F4.imprint","IMPRINT",EDGE,{"derivedFrom":subQ6}),-1.0]])]});}
            extrude(context, id + "F8", {"entities" : qUnion([Q0, Q1, Q2, Q3]), "operationType" : NewBodyOperationType.ADD, "oppositeDirection" : true, "depth" : 2 * mm, "offsetDistance" : 25 * mm});
        }
        {
            var Q0;
            {var subQ0=sQuery(id+"F0.wireOp",EDGE,"E8");var subQ1=sQuery(id+"F0.wireOp",EDGE,"E7");var subQ2=sQuery(id+"F0.wireOp",EDGE,"E6");var subQ3=sQuery(id+"F0.wireOp",EDGE,"E9");var subQ4=sQuery(id+"F0.wireOp",EDGE,"E5");var subQ5=sQuery(id+"F0.wireOp",EDGE,"E1");Q0=makeQuery(id+"F8.boolean.opBoolean","MERGE",FACE,{"derivedFrom":[makeQuery(id+"F1.opExtrude","CAP_FACE",FACE,{"disambiguationData":[OSD([subQ5,subQ4,subQ2,subQ1,subQ0,subQ3,sQuery(id+"F0.wireOp",EDGE,"E10"),sQuery(id+"F0.wireOp",EDGE,"E11"),sQuery(id+"F0.wireOp",EDGE,"E12"),sQuery(id+"F0.wireOp",EDGE,"E13"),sQuery(id+"F0.wireOp",EDGE,"E15.MirrorC"),sQuery(id+"F0.wireOp",EDGE,"E16.MirrorC"),sQuery(id+"F0.wireOp",EDGE,"E19"),sQuery(id+"F0.wireOp",EDGE,"E20"),sQuery(id+"F0.wireOp",EDGE,"E21"),sQuery(id+"F0.wireOp",EDGE,"E22"),sQuery(id+"F0.wireOp",EDGE,"E27"),sQuery(id+"F0.wireOp",EDGE,"E26"),sQuery(id+"F0.wireOp",EDGE,"E23"),sQuery(id+"F0.wireOp",EDGE,"E28.MirrorC"),sQuery(id+"F0.wireOp",EDGE,"E29.MirrorC"),sQuery(id+"F0.wireOp",EDGE,"E30.MirrorC"),sQuery(id+"F0.wireOp",EDGE,"E34"),sQuery(id+"F0.wireOp",EDGE,"E35"),sQuery(id+"F0.wireOp",EDGE,"E36"),sQuery(id+"F0.wireOp",EDGE,"E37")])],"isStart":false}),makeQuery(id+"F8.opExtrude","CAP_FACE",FACE,{"disambiguationData":[OSD([sQuery(id+"F4.wireOp",EDGE,"E112"),sQuery(id+"F4.wireOp",EDGE,"E114"),sQuery(id+"F4.wireOp",EDGE,"E115"),sQuery(id+"F4.wireOp",EDGE,"E116")])],"isStart":true}),makeQuery(id+"F8.opExtrude","CAP_FACE",FACE,{"disambiguationData":[OSD([subQ5,subQ0,sQuery(id+"F4.wireOp",EDGE,"E117"),sQuery(id+"F4.wireOp",EDGE,"E118")])],"isStart":true}),makeQuery(id+"F8.opExtrude","CAP_FACE",FACE,{"disambiguationData":[OSD([subQ4,subQ2,subQ3,sQuery(id+"F4.wireOp",EDGE,"E124"),sQuery(id+"F4.wireOp",EDGE,"E125")])],"isStart":true}),makeQuery(id+"F8.opExtrude","CAP_FACE",FACE,{"disambiguationData":[OSD([subQ2,subQ1,subQ0,sQuery(id+"F4.wireOp",EDGE,"E133"),sQuery(id+"F4.wireOp",EDGE,"E134")])],"isStart":true})]});}
            var sketch = newSketch(context, id + "F9", { "sketchPlane" : qUnion([Q0])});
            skLineSegment(sketch, "E145.bottom", {"start": v(-194.5, 64.5) * mm, "end": v(194.5, 64.5) * mm, "construction": true});
            skLineSegment(sketch, "E145.top", {"start": v(-194.5, -280.5) * mm, "end": v(194.5, -280.5) * mm, "construction": true});
            skLineSegment(sketch, "E145.left", {"start": v(-194.5, 64.5) * mm, "end": v(-194.5, -280.5) * mm, "construction": true});
            skLineSegment(sketch, "E145.right", {"start": v(194.5, 64.5) * mm, "end": v(194.5, -280.5) * mm, "construction": true});
            skLineSegment(sketch, "E146", {"start": v(-109, -280.5) * mm, "end": v(109, -280.5) * mm});
            skLineSegment(sketch, "E147", {"start": v(-194.5, -108) * mm, "end": v(245.75, -108) * mm, "construction": true});
            skPoint(sketch, "E147.endSnap0", {"position": v(194.5, -108) * mm});
            skLineSegment(sketch, "E148.MirrorCS", {"start": v(-109, 64.5) * mm, "end": v(109, 64.5) * mm});
            skLineSegment(sketch, "E149", {"start": v(-194.5, -21) * mm, "end": v(-194.5, -195) * mm});
            skLineSegment(sketch, "E150", {"start": v(-75.12, 57.5) * mm, "end": v(75.12, 57.5) * mm});
            skLineSegment(sketch, "E151", {"start": v(-187.5, -54.88) * mm, "end": v(-187.5, -161.12) * mm});
            skLineSegment(sketch, "E152.MirrorCS", {"start": v(187.5, -54.88) * mm, "end": v(187.5, -161.12) * mm});
            skLineSegment(sketch, "E153.MirrorCS", {"start": v(194.5, -21) * mm, "end": v(194.5, -195) * mm});
            skLineSegment(sketch, "E154", {"start": v(-134, -102.76) * mm, "end": v(-134, -113.24) * mm});
            skLineSegment(sketch, "E155", {"start": v(-84, -102.76) * mm, "end": v(-84, -113.24) * mm});
            skLineSegment(sketch, "E156", {"start": v(-109, 64.5) * mm, "end": v(-109, -280.5) * mm, "construction": true});
            skLineSegment(sketch, "E157.MirrorCS", {"start": v(84, -102.76) * mm, "end": v(84, -113.24) * mm});
            skLineSegment(sketch, "E158.MirrorCS", {"start": v(134, -102.76) * mm, "end": v(134, -113.24) * mm});
            skArc(sketch, "E159", {"start": v(-75.12, 57.5) * mm, "mid": v(-91.7, 62.73) * mm, "end": v(-109, 64.5) * mm});
            skArc(sketch, "E160", {"start": v(-187.5, -54.88) * mm, "mid": v(-192.73, -38.3) * mm, "end": v(-194.5, -21) * mm});
            skArc(sketch, "E161", {"start": v(-134, -102.76) * mm, "mid": v(-109, -106.5) * mm, "end": v(-84, -102.76) * mm});
            skArc(sketch, "E162", {"start": v(-84, -113.24) * mm, "mid": v(-109, -109.5) * mm, "end": v(-134, -113.24) * mm});
            skArc(sketch, "E163", {"start": v(-187.5, -161.12) * mm, "mid": v(-192.73, -177.7) * mm, "end": v(-194.5, -195) * mm});
            skArc(sketch, "E164", {"start": v(-109, -280.5) * mm, "mid": v(-95.58, -279.44) * mm, "end": v(-82.5, -276.29) * mm});
            skArc(sketch, "E165", {"start": v(187.5, -161.12) * mm, "mid": v(192.73, -177.7) * mm, "end": v(194.5, -195) * mm});
            skArc(sketch, "E166", {"start": v(109, -280.5) * mm, "mid": v(95.58, -279.44) * mm, "end": v(82.5, -276.29) * mm});
            skArc(sketch, "E167.MirrorCS", {"start": v(84, -113.24) * mm, "mid": v(109, -109.5) * mm, "end": v(134, -113.24) * mm});
            skArc(sketch, "E168.MirrorCS", {"start": v(134, -102.76) * mm, "mid": v(109, -106.5) * mm, "end": v(84, -102.76) * mm});
            skArc(sketch, "E169", {"start": v(194.5, -21) * mm, "mid": v(192.73, -38.3) * mm, "end": v(187.5, -54.88) * mm});
            skArc(sketch, "E170", {"start": v(109, 64.5) * mm, "mid": v(91.7, 62.73) * mm, "end": v(75.12, 57.5) * mm});
            skSolve(sketch);
        }
        {
            var Q0;
            {var subQ0=sQuery(id+"F0.wireOp",EDGE,"E8");var subQ1=sQuery(id+"F0.wireOp",EDGE,"E7");var subQ2=sQuery(id+"F0.wireOp",EDGE,"E6");var subQ3=sQuery(id+"F0.wireOp",EDGE,"E9");var subQ4=sQuery(id+"F0.wireOp",EDGE,"E5");var subQ5=sQuery(id+"F0.wireOp",EDGE,"E1");Q0=makeQuery(id+"F8.boolean.opBoolean","MERGE",FACE,{"derivedFrom":[makeQuery(id+"F1.opExtrude","CAP_FACE",FACE,{"disambiguationData":[OSD([subQ5,subQ4,subQ2,subQ1,subQ0,subQ3,sQuery(id+"F0.wireOp",EDGE,"E10"),sQuery(id+"F0.wireOp",EDGE,"E11"),sQuery(id+"F0.wireOp",EDGE,"E12"),sQuery(id+"F0.wireOp",EDGE,"E13"),sQuery(id+"F0.wireOp",EDGE,"E15.MirrorC"),sQuery(id+"F0.wireOp",EDGE,"E16.MirrorC"),sQuery(id+"F0.wireOp",EDGE,"E19"),sQuery(id+"F0.wireOp",EDGE,"E20"),sQuery(id+"F0.wireOp",EDGE,"E21"),sQuery(id+"F0.wireOp",EDGE,"E22"),sQuery(id+"F0.wireOp",EDGE,"E27"),sQuery(id+"F0.wireOp",EDGE,"E26"),sQuery(id+"F0.wireOp",EDGE,"E23"),sQuery(id+"F0.wireOp",EDGE,"E28.MirrorC"),sQuery(id+"F0.wireOp",EDGE,"E29.MirrorC"),sQuery(id+"F0.wireOp",EDGE,"E30.MirrorC"),sQuery(id+"F0.wireOp",EDGE,"E34"),sQuery(id+"F0.wireOp",EDGE,"E35"),sQuery(id+"F0.wireOp",EDGE,"E36"),sQuery(id+"F0.wireOp",EDGE,"E37")])],"isStart":false}),makeQuery(id+"F8.opExtrude","CAP_FACE",FACE,{"disambiguationData":[OSD([sQuery(id+"F4.wireOp",EDGE,"E112"),sQuery(id+"F4.wireOp",EDGE,"E114"),sQuery(id+"F4.wireOp",EDGE,"E115"),sQuery(id+"F4.wireOp",EDGE,"E116")])],"isStart":true}),makeQuery(id+"F8.opExtrude","CAP_FACE",FACE,{"disambiguationData":[OSD([subQ5,subQ0,sQuery(id+"F4.wireOp",EDGE,"E117"),sQuery(id+"F4.wireOp",EDGE,"E118")])],"isStart":true}),makeQuery(id+"F8.opExtrude","CAP_FACE",FACE,{"disambiguationData":[OSD([subQ4,subQ2,subQ3,sQuery(id+"F4.wireOp",EDGE,"E124"),sQuery(id+"F4.wireOp",EDGE,"E125")])],"isStart":true}),makeQuery(id+"F8.opExtrude","CAP_FACE",FACE,{"disambiguationData":[OSD([subQ2,subQ1,subQ0,sQuery(id+"F4.wireOp",EDGE,"E133"),sQuery(id+"F4.wireOp",EDGE,"E134")])],"isStart":true})]});}
            var sketch = newSketch(context, id + "F10", { "sketchPlane" : qUnion([Q0])});
            skCircle(sketch, "E171.cCircle", {"center": v(-109, -21) * mm, "radius": 83 * mm, "construction": true});
            skLineSegment(sketch, "E171.0", {"start": v(-140.76, 55.68) * mm, "end": v(-77.24, 55.68) * mm, "construction": true});
            skLineSegment(sketch, "E171.1", {"start": v(-77.24, 55.68) * mm, "end": v(-32.32, 10.76) * mm, "construction": true});
            skLineSegment(sketch, "E171.2", {"start": v(-32.32, 10.76) * mm, "end": v(-32.32, -52.76) * mm, "construction": true});
            skLineSegment(sketch, "E171.3", {"start": v(-32.32, -52.76) * mm, "end": v(-77.24, -97.68) * mm, "construction": true});
            skLineSegment(sketch, "E171.4", {"start": v(-77.24, -97.68) * mm, "end": v(-140.76, -97.68) * mm, "construction": true});
            skLineSegment(sketch, "E171.5", {"start": v(-140.76, -97.68) * mm, "end": v(-185.68, -52.76) * mm, "construction": true});
            skLineSegment(sketch, "E171.6", {"start": v(-185.68, -52.76) * mm, "end": v(-185.68, 10.76) * mm, "construction": true});
            skLineSegment(sketch, "E171.7", {"start": v(-185.68, 10.76) * mm, "end": v(-140.76, 55.68) * mm, "construction": true});
            skLineSegment(sketch, "E172", {"start": v(-140.76, 55.68) * mm, "end": v(-77.24, -97.68) * mm, "construction": true});
            skCircle(sketch, "E173", {"center": v(-140.76, 55.68) * mm, "radius": 1.25 * mm});
            skCircle(sketch, "E174.1.0", {"center": v(-185.68, 10.76) * mm, "radius": 1.25 * mm});
            skCircle(sketch, "E174.2.0", {"center": v(-185.68, -52.76) * mm, "radius": 1.25 * mm});
            skCircle(sketch, "E174.3.0", {"center": v(-140.76, -97.68) * mm, "radius": 1.25 * mm});
            skCircle(sketch, "E174.4.0", {"center": v(-77.24, -97.68) * mm, "radius": 1.25 * mm});
            skCircle(sketch, "E174.5.0", {"center": v(-32.32, -52.76) * mm, "radius": 1.25 * mm});
            skCircle(sketch, "E174.6.0", {"center": v(-32.32, 10.76) * mm, "radius": 1.25 * mm});
            skCircle(sketch, "E174.7.0", {"center": v(-77.24, 55.68) * mm, "radius": 1.25 * mm});
            skLineSegment(sketch, "E175", {"start": v(-109, 55.68) * mm, "end": v(-109, -97.68) * mm, "construction": true});
            skLineSegment(sketch, "E176.1.0", {"start": v(-185.68, 10.76) * mm, "end": v(-32.32, -52.76) * mm, "construction": true});
            skLineSegment(sketch, "E176.2.0", {"start": v(-185.68, -52.76) * mm, "end": v(-32.32, 10.76) * mm, "construction": true});
            skLineSegment(sketch, "E176.3.0", {"start": v(-140.76, -97.68) * mm, "end": v(-77.24, 55.68) * mm, "construction": true});
            skLineSegment(sketch, "E177.2.4.0", {"start": v(-77.24, -97.68) * mm, "end": v(-140.76, 55.68) * mm, "construction": true});
            skLineSegment(sketch, "E177.2.5.0", {"start": v(-32.32, -52.76) * mm, "end": v(-185.68, 10.76) * mm, "construction": true});
            skLineSegment(sketch, "E177.2.6.0", {"start": v(-32.32, 10.76) * mm, "end": v(-185.68, -52.76) * mm, "construction": true});
            skLineSegment(sketch, "E177.2.7.0", {"start": v(-77.24, 55.68) * mm, "end": v(-140.76, -97.68) * mm, "construction": true});
            skCircle(sketch, "E178", {"center": v(-109, -21) * mm, "radius": 2.5 * mm});
            skCircle(sketch, "E179", {"center": v(-109, -21) * mm, "radius": 7.5 * mm});
            skLineSegment(sketch, "E180", {"start": v(-81.28, 52.44) * mm, "end": v(-108.6, -13.51) * mm});
            skLineSegment(sketch, "E181.MirrorCS", {"start": v(-76.66, 50.53) * mm, "end": v(-103.98, -15.42) * mm});
            skArc(sketch, "E182", {"start": v(-81.28, 52.44) * mm, "mid": v(-78.96, 51.52) * mm, "end": v(-76.66, 50.53) * mm});
            skLineSegment(sketch, "E183.1.0", {"start": v(-136.72, 52.44) * mm, "end": v(-109.4, -13.51) * mm});
            skArc(sketch, "E183.1.1", {"start": v(-141.34, 50.53) * mm, "mid": v(-139.04, 51.52) * mm, "end": v(-136.72, 52.44) * mm});
            skLineSegment(sketch, "E183.1.2", {"start": v(-141.34, 50.53) * mm, "end": v(-114.02, -15.42) * mm});
            skLineSegment(sketch, "E183.2.0", {"start": v(-180.53, 11.34) * mm, "end": v(-114.58, -15.98) * mm});
            skArc(sketch, "E183.2.1", {"start": v(-182.44, 6.72) * mm, "mid": v(-181.52, 9.04) * mm, "end": v(-180.53, 11.34) * mm});
            skLineSegment(sketch, "E183.2.2", {"start": v(-182.44, 6.72) * mm, "end": v(-116.49, -20.6) * mm});
            skLineSegment(sketch, "E183.3.0", {"start": v(-182.44, -48.72) * mm, "end": v(-116.49, -21.4) * mm});
            skArc(sketch, "E183.3.1", {"start": v(-180.53, -53.34) * mm, "mid": v(-181.52, -51.04) * mm, "end": v(-182.44, -48.72) * mm});
            skLineSegment(sketch, "E183.3.2", {"start": v(-180.53, -53.34) * mm, "end": v(-114.58, -26.02) * mm});
            skLineSegment(sketch, "E183.4.0", {"start": v(-141.34, -92.53) * mm, "end": v(-114.02, -26.58) * mm});
            skArc(sketch, "E183.4.1", {"start": v(-136.72, -94.44) * mm, "mid": v(-139.04, -93.52) * mm, "end": v(-141.34, -92.53) * mm});
            skLineSegment(sketch, "E183.4.2", {"start": v(-136.72, -94.44) * mm, "end": v(-109.4, -28.49) * mm});
            skLineSegment(sketch, "E183.5.0", {"start": v(-81.28, -94.44) * mm, "end": v(-108.6, -28.49) * mm});
            skArc(sketch, "E183.5.1", {"start": v(-76.66, -92.53) * mm, "mid": v(-78.96, -93.52) * mm, "end": v(-81.28, -94.44) * mm});
            skLineSegment(sketch, "E183.5.2", {"start": v(-76.66, -92.53) * mm, "end": v(-103.98, -26.58) * mm});
            skLineSegment(sketch, "E183.6.0", {"start": v(-37.47, -53.34) * mm, "end": v(-103.42, -26.02) * mm});
            skArc(sketch, "E183.6.1", {"start": v(-35.56, -48.72) * mm, "mid": v(-36.48, -51.04) * mm, "end": v(-37.47, -53.34) * mm});
            skLineSegment(sketch, "E183.6.2", {"start": v(-35.56, -48.72) * mm, "end": v(-101.51, -21.4) * mm});
            skLineSegment(sketch, "E183.7.0", {"start": v(-35.56, 6.72) * mm, "end": v(-101.51, -20.6) * mm});
            skArc(sketch, "E183.7.1", {"start": v(-37.47, 11.34) * mm, "mid": v(-36.48, 9.04) * mm, "end": v(-35.56, 6.72) * mm});
            skLineSegment(sketch, "E183.7.2", {"start": v(-37.47, 11.34) * mm, "end": v(-103.42, -15.98) * mm});
            skLineSegment(sketch, "E184.0.1.0", {"start": v(-109, -118.32) * mm, "end": v(-109, -271.68) * mm, "construction": true});
            skCircle(sketch, "E184.0.1.1", {"center": v(-109, -195) * mm, "radius": 83 * mm, "construction": true});
            skLineSegment(sketch, "E184.0.1.2", {"start": v(-185.68, -226.76) * mm, "end": v(-32.32, -163.24) * mm, "construction": true});
            skLineSegment(sketch, "E184.0.1.3", {"start": v(-32.32, -226.76) * mm, "end": v(-77.24, -271.68) * mm, "construction": true});
            skLineSegment(sketch, "E184.0.1.4", {"start": v(-182.44, -167.28) * mm, "end": v(-116.49, -194.6) * mm});
            skLineSegment(sketch, "E184.0.1.5", {"start": v(-141.34, -123.47) * mm, "end": v(-114.02, -189.42) * mm});
            skLineSegment(sketch, "E184.0.1.6", {"start": v(-37.47, -162.66) * mm, "end": v(-103.42, -189.98) * mm});
            skLineSegment(sketch, "E184.0.1.7", {"start": v(-81.28, -121.56) * mm, "end": v(-108.6, -187.51) * mm});
            skLineSegment(sketch, "E184.0.1.8", {"start": v(-32.32, -163.24) * mm, "end": v(-32.32, -226.76) * mm, "construction": true});
            skLineSegment(sketch, "E184.0.1.9", {"start": v(-77.24, -118.32) * mm, "end": v(-32.32, -163.24) * mm, "construction": true});
            skLineSegment(sketch, "E184.0.1.10", {"start": v(-76.66, -123.47) * mm, "end": v(-103.98, -189.42) * mm});
            skLineSegment(sketch, "E184.0.1.11", {"start": v(-140.76, -118.32) * mm, "end": v(-77.24, -118.32) * mm, "construction": true});
            skLineSegment(sketch, "E184.0.1.12", {"start": v(-37.47, -227.34) * mm, "end": v(-103.42, -200.02) * mm});
            skLineSegment(sketch, "E184.0.1.13", {"start": v(-136.72, -268.44) * mm, "end": v(-109.4, -202.49) * mm});
            skLineSegment(sketch, "E184.0.1.14", {"start": v(-136.72, -121.56) * mm, "end": v(-109.4, -187.51) * mm});
            skLineSegment(sketch, "E184.0.1.15", {"start": v(-141.34, -266.53) * mm, "end": v(-114.02, -200.58) * mm});
            skLineSegment(sketch, "E184.0.1.16", {"start": v(-35.56, -222.72) * mm, "end": v(-101.51, -195.4) * mm});
            skLineSegment(sketch, "E184.0.1.17", {"start": v(-140.76, -271.68) * mm, "end": v(-185.68, -226.76) * mm, "construction": true});
            skLineSegment(sketch, "E184.0.1.18", {"start": v(-180.53, -227.34) * mm, "end": v(-114.58, -200.02) * mm});
            skLineSegment(sketch, "E184.0.1.19", {"start": v(-76.66, -266.53) * mm, "end": v(-103.98, -200.58) * mm});
            skLineSegment(sketch, "E184.0.1.20", {"start": v(-180.53, -162.66) * mm, "end": v(-114.58, -189.98) * mm});
            skLineSegment(sketch, "E184.0.1.21", {"start": v(-35.56, -167.28) * mm, "end": v(-101.51, -194.6) * mm});
            skLineSegment(sketch, "E184.0.1.22", {"start": v(-182.44, -222.72) * mm, "end": v(-116.49, -195.4) * mm});
            skLineSegment(sketch, "E184.0.1.23", {"start": v(-185.68, -163.24) * mm, "end": v(-140.76, -118.32) * mm, "construction": true});
            skLineSegment(sketch, "E184.0.1.24", {"start": v(-185.68, -163.24) * mm, "end": v(-32.32, -226.76) * mm, "construction": true});
            skLineSegment(sketch, "E184.0.1.25", {"start": v(-185.68, -226.76) * mm, "end": v(-185.68, -163.24) * mm, "construction": true});
            skLineSegment(sketch, "E184.0.1.26", {"start": v(-81.28, -268.44) * mm, "end": v(-108.6, -202.49) * mm});
            skLineSegment(sketch, "E184.0.1.27", {"start": v(-77.24, -271.68) * mm, "end": v(-140.76, -271.68) * mm, "construction": true});
            skPoint(sketch, "E184.0.1.28", {"position": v(-109, -195) * mm});
            skLineSegment(sketch, "E184.0.1.29", {"start": v(-140.76, -118.32) * mm, "end": v(-77.24, -271.68) * mm, "construction": true});
            skLineSegment(sketch, "E184.0.1.30", {"start": v(-77.24, -118.32) * mm, "end": v(-140.76, -271.68) * mm, "construction": true});
            skLineSegment(sketch, "E184.0.1.31", {"start": v(-140.76, -271.68) * mm, "end": v(-77.24, -118.32) * mm, "construction": true});
            skLineSegment(sketch, "E184.0.1.32", {"start": v(-32.32, -226.76) * mm, "end": v(-185.68, -163.24) * mm, "construction": true});
            skPoint(sketch, "E184.0.1.33", {"position": v(-109, -195) * mm});
            skLineSegment(sketch, "E184.0.1.34", {"start": v(-77.24, -271.68) * mm, "end": v(-140.76, -118.32) * mm, "construction": true});
            skLineSegment(sketch, "E184.0.1.35", {"start": v(-32.32, -163.24) * mm, "end": v(-185.68, -226.76) * mm, "construction": true});
            skPoint(sketch, "E184.0.1.36", {"position": v(-109, -195) * mm});
            skCircle(sketch, "E184.0.1.37", {"center": v(-109, -195) * mm, "radius": 7.5 * mm});
            skCircle(sketch, "E184.0.1.38", {"center": v(-185.68, -163.24) * mm, "radius": 1.25 * mm});
            skArc(sketch, "E184.0.1.39", {"start": v(-180.53, -227.34) * mm, "mid": v(-181.52, -225.04) * mm, "end": v(-182.44, -222.72) * mm});
            skCircle(sketch, "E184.0.1.40", {"center": v(-32.32, -163.24) * mm, "radius": 1.25 * mm});
            skCircle(sketch, "E184.0.1.41", {"center": v(-185.68, -226.76) * mm, "radius": 1.25 * mm});
            skArc(sketch, "E184.0.1.42", {"start": v(-81.28, -121.56) * mm, "mid": v(-78.96, -122.48) * mm, "end": v(-76.66, -123.47) * mm});
            skArc(sketch, "E184.0.1.43", {"start": v(-141.34, -123.47) * mm, "mid": v(-139.04, -122.48) * mm, "end": v(-136.72, -121.56) * mm});
            skArc(sketch, "E184.0.1.44", {"start": v(-136.72, -268.44) * mm, "mid": v(-139.04, -267.52) * mm, "end": v(-141.34, -266.53) * mm});
            skArc(sketch, "E184.0.1.45", {"start": v(-37.47, -162.66) * mm, "mid": v(-36.48, -164.96) * mm, "end": v(-35.56, -167.28) * mm});
            skArc(sketch, "E184.0.1.46", {"start": v(-182.44, -167.28) * mm, "mid": v(-181.52, -164.96) * mm, "end": v(-180.53, -162.66) * mm});
            skCircle(sketch, "E184.0.1.47", {"center": v(-140.76, -118.32) * mm, "radius": 1.25 * mm});
            skCircle(sketch, "E184.0.1.48", {"center": v(-77.24, -118.32) * mm, "radius": 1.25 * mm});
            skCircle(sketch, "E184.0.1.49", {"center": v(-32.32, -226.76) * mm, "radius": 1.25 * mm});
            skArc(sketch, "E184.0.1.50", {"start": v(-35.56, -222.72) * mm, "mid": v(-36.48, -225.04) * mm, "end": v(-37.47, -227.34) * mm});
            skCircle(sketch, "E184.0.1.51", {"center": v(-140.76, -271.68) * mm, "radius": 1.25 * mm});
            skCircle(sketch, "E184.0.1.52", {"center": v(-77.24, -271.68) * mm, "radius": 1.25 * mm});
            skArc(sketch, "E184.0.1.53", {"start": v(-76.66, -266.53) * mm, "mid": v(-78.96, -267.52) * mm, "end": v(-81.28, -268.44) * mm});
            skCircle(sketch, "E184.0.1.54", {"center": v(-109, -195) * mm, "radius": 2.5 * mm});
            skLineSegment(sketch, "E184.1.0.0", {"start": v(109, 55.68) * mm, "end": v(109, -97.68) * mm, "construction": true});
            skCircle(sketch, "E184.1.0.1", {"center": v(109, -21) * mm, "radius": 83 * mm, "construction": true});
            skLineSegment(sketch, "E184.1.0.2", {"start": v(32.32, -52.76) * mm, "end": v(185.68, 10.76) * mm, "construction": true});
            skLineSegment(sketch, "E184.1.0.3", {"start": v(185.68, -52.76) * mm, "end": v(140.76, -97.68) * mm, "construction": true});
            skLineSegment(sketch, "E184.1.0.4", {"start": v(35.56, 6.72) * mm, "end": v(101.51, -20.6) * mm});
            skLineSegment(sketch, "E184.1.0.5", {"start": v(76.66, 50.53) * mm, "end": v(103.98, -15.42) * mm});
            skLineSegment(sketch, "E184.1.0.6", {"start": v(180.53, 11.34) * mm, "end": v(114.58, -15.98) * mm});
            skLineSegment(sketch, "E184.1.0.7", {"start": v(136.72, 52.44) * mm, "end": v(109.4, -13.51) * mm});
            skLineSegment(sketch, "E184.1.0.8", {"start": v(185.68, 10.76) * mm, "end": v(185.68, -52.76) * mm, "construction": true});
            skLineSegment(sketch, "E184.1.0.9", {"start": v(140.76, 55.68) * mm, "end": v(185.68, 10.76) * mm, "construction": true});
            skLineSegment(sketch, "E184.1.0.10", {"start": v(141.34, 50.53) * mm, "end": v(114.02, -15.42) * mm});
            skLineSegment(sketch, "E184.1.0.11", {"start": v(77.24, 55.68) * mm, "end": v(140.76, 55.68) * mm, "construction": true});
            skLineSegment(sketch, "E184.1.0.12", {"start": v(180.53, -53.34) * mm, "end": v(114.58, -26.02) * mm});
            skLineSegment(sketch, "E184.1.0.13", {"start": v(81.28, -94.44) * mm, "end": v(108.6, -28.49) * mm});
            skLineSegment(sketch, "E184.1.0.14", {"start": v(81.28, 52.44) * mm, "end": v(108.6, -13.51) * mm});
            skLineSegment(sketch, "E184.1.0.15", {"start": v(76.66, -92.53) * mm, "end": v(103.98, -26.58) * mm});
            skLineSegment(sketch, "E184.1.0.16", {"start": v(182.44, -48.72) * mm, "end": v(116.49, -21.4) * mm});
            skLineSegment(sketch, "E184.1.0.17", {"start": v(77.24, -97.68) * mm, "end": v(32.32, -52.76) * mm, "construction": true});
            skLineSegment(sketch, "E184.1.0.18", {"start": v(37.47, -53.34) * mm, "end": v(103.42, -26.02) * mm});
            skLineSegment(sketch, "E184.1.0.19", {"start": v(141.34, -92.53) * mm, "end": v(114.02, -26.58) * mm});
            skLineSegment(sketch, "E184.1.0.20", {"start": v(37.47, 11.34) * mm, "end": v(103.42, -15.98) * mm});
            skLineSegment(sketch, "E184.1.0.21", {"start": v(182.44, 6.72) * mm, "end": v(116.49, -20.6) * mm});
            skLineSegment(sketch, "E184.1.0.22", {"start": v(35.56, -48.72) * mm, "end": v(101.51, -21.4) * mm});
            skLineSegment(sketch, "E184.1.0.23", {"start": v(32.32, 10.76) * mm, "end": v(77.24, 55.68) * mm, "construction": true});
            skLineSegment(sketch, "E184.1.0.24", {"start": v(32.32, 10.76) * mm, "end": v(185.68, -52.76) * mm, "construction": true});
            skLineSegment(sketch, "E184.1.0.25", {"start": v(32.32, -52.76) * mm, "end": v(32.32, 10.76) * mm, "construction": true});
            skLineSegment(sketch, "E184.1.0.26", {"start": v(136.72, -94.44) * mm, "end": v(109.4, -28.49) * mm});
            skLineSegment(sketch, "E184.1.0.27", {"start": v(140.76, -97.68) * mm, "end": v(77.24, -97.68) * mm, "construction": true});
            skPoint(sketch, "E184.1.0.28", {"position": v(109, -21) * mm});
            skLineSegment(sketch, "E184.1.0.29", {"start": v(77.24, 55.68) * mm, "end": v(140.76, -97.68) * mm, "construction": true});
            skLineSegment(sketch, "E184.1.0.30", {"start": v(140.76, 55.68) * mm, "end": v(77.24, -97.68) * mm, "construction": true});
            skLineSegment(sketch, "E184.1.0.31", {"start": v(77.24, -97.68) * mm, "end": v(140.76, 55.68) * mm, "construction": true});
            skLineSegment(sketch, "E184.1.0.32", {"start": v(185.68, -52.76) * mm, "end": v(32.32, 10.76) * mm, "construction": true});
            skPoint(sketch, "E184.1.0.33", {"position": v(109, -21) * mm});
            skLineSegment(sketch, "E184.1.0.34", {"start": v(140.76, -97.68) * mm, "end": v(77.24, 55.68) * mm, "construction": true});
            skLineSegment(sketch, "E184.1.0.35", {"start": v(185.68, 10.76) * mm, "end": v(32.32, -52.76) * mm, "construction": true});
            skPoint(sketch, "E184.1.0.36", {"position": v(109, -21) * mm});
            skCircle(sketch, "E184.1.0.37", {"center": v(109, -21) * mm, "radius": 7.5 * mm});
            skCircle(sketch, "E184.1.0.38", {"center": v(32.32, 10.76) * mm, "radius": 1.25 * mm});
            skArc(sketch, "E184.1.0.39", {"start": v(37.47, -53.34) * mm, "mid": v(36.48, -51.04) * mm, "end": v(35.56, -48.72) * mm});
            skCircle(sketch, "E184.1.0.40", {"center": v(185.68, 10.76) * mm, "radius": 1.25 * mm});
            skCircle(sketch, "E184.1.0.41", {"center": v(32.32, -52.76) * mm, "radius": 1.25 * mm});
            skArc(sketch, "E184.1.0.42", {"start": v(136.72, 52.44) * mm, "mid": v(139.04, 51.52) * mm, "end": v(141.34, 50.53) * mm});
            skArc(sketch, "E184.1.0.43", {"start": v(76.66, 50.53) * mm, "mid": v(78.96, 51.52) * mm, "end": v(81.28, 52.44) * mm});
            skArc(sketch, "E184.1.0.44", {"start": v(81.28, -94.44) * mm, "mid": v(78.96, -93.52) * mm, "end": v(76.66, -92.53) * mm});
            skArc(sketch, "E184.1.0.45", {"start": v(180.53, 11.34) * mm, "mid": v(181.52, 9.04) * mm, "end": v(182.44, 6.72) * mm});
            skArc(sketch, "E184.1.0.46", {"start": v(35.56, 6.72) * mm, "mid": v(36.48, 9.04) * mm, "end": v(37.47, 11.34) * mm});
            skCircle(sketch, "E184.1.0.47", {"center": v(77.24, 55.68) * mm, "radius": 1.25 * mm});
            skCircle(sketch, "E184.1.0.48", {"center": v(140.76, 55.68) * mm, "radius": 1.25 * mm});
            skCircle(sketch, "E184.1.0.49", {"center": v(185.68, -52.76) * mm, "radius": 1.25 * mm});
            skArc(sketch, "E184.1.0.50", {"start": v(182.44, -48.72) * mm, "mid": v(181.52, -51.04) * mm, "end": v(180.53, -53.34) * mm});
            skCircle(sketch, "E184.1.0.51", {"center": v(77.24, -97.68) * mm, "radius": 1.25 * mm});
            skCircle(sketch, "E184.1.0.52", {"center": v(140.76, -97.68) * mm, "radius": 1.25 * mm});
            skArc(sketch, "E184.1.0.53", {"start": v(141.34, -92.53) * mm, "mid": v(139.04, -93.52) * mm, "end": v(136.72, -94.44) * mm});
            skCircle(sketch, "E184.1.0.54", {"center": v(109, -21) * mm, "radius": 2.5 * mm});
            skLineSegment(sketch, "E184.1.1.0", {"start": v(109, -118.32) * mm, "end": v(109, -271.68) * mm, "construction": true});
            skCircle(sketch, "E184.1.1.1", {"center": v(109, -195) * mm, "radius": 83 * mm, "construction": true});
            skLineSegment(sketch, "E184.1.1.2", {"start": v(32.32, -226.76) * mm, "end": v(185.68, -163.24) * mm, "construction": true});
            skLineSegment(sketch, "E184.1.1.3", {"start": v(185.68, -226.76) * mm, "end": v(140.76, -271.68) * mm, "construction": true});
            skLineSegment(sketch, "E184.1.1.4", {"start": v(35.56, -167.28) * mm, "end": v(101.51, -194.6) * mm});
            skLineSegment(sketch, "E184.1.1.5", {"start": v(76.66, -123.47) * mm, "end": v(103.98, -189.42) * mm});
            skLineSegment(sketch, "E184.1.1.6", {"start": v(180.53, -162.66) * mm, "end": v(114.58, -189.98) * mm});
            skLineSegment(sketch, "E184.1.1.7", {"start": v(136.72, -121.56) * mm, "end": v(109.4, -187.51) * mm});
            skLineSegment(sketch, "E184.1.1.8", {"start": v(185.68, -163.24) * mm, "end": v(185.68, -226.76) * mm, "construction": true});
            skLineSegment(sketch, "E184.1.1.9", {"start": v(140.76, -118.32) * mm, "end": v(185.68, -163.24) * mm, "construction": true});
            skLineSegment(sketch, "E184.1.1.10", {"start": v(141.34, -123.47) * mm, "end": v(114.02, -189.42) * mm});
            skLineSegment(sketch, "E184.1.1.11", {"start": v(77.24, -118.32) * mm, "end": v(140.76, -118.32) * mm, "construction": true});
            skLineSegment(sketch, "E184.1.1.12", {"start": v(180.53, -227.34) * mm, "end": v(114.58, -200.02) * mm});
            skLineSegment(sketch, "E184.1.1.13", {"start": v(81.28, -268.44) * mm, "end": v(108.6, -202.49) * mm});
            skLineSegment(sketch, "E184.1.1.14", {"start": v(81.28, -121.56) * mm, "end": v(108.6, -187.51) * mm});
            skLineSegment(sketch, "E184.1.1.15", {"start": v(76.66, -266.53) * mm, "end": v(103.98, -200.58) * mm});
            skLineSegment(sketch, "E184.1.1.16", {"start": v(182.44, -222.72) * mm, "end": v(116.49, -195.4) * mm});
            skLineSegment(sketch, "E184.1.1.17", {"start": v(77.24, -271.68) * mm, "end": v(32.32, -226.76) * mm, "construction": true});
            skLineSegment(sketch, "E184.1.1.18", {"start": v(37.47, -227.34) * mm, "end": v(103.42, -200.02) * mm});
            skLineSegment(sketch, "E184.1.1.19", {"start": v(141.34, -266.53) * mm, "end": v(114.02, -200.58) * mm});
            skLineSegment(sketch, "E184.1.1.20", {"start": v(37.47, -162.66) * mm, "end": v(103.42, -189.98) * mm});
            skLineSegment(sketch, "E184.1.1.21", {"start": v(182.44, -167.28) * mm, "end": v(116.49, -194.6) * mm});
            skLineSegment(sketch, "E184.1.1.22", {"start": v(35.56, -222.72) * mm, "end": v(101.51, -195.4) * mm});
            skLineSegment(sketch, "E184.1.1.23", {"start": v(32.32, -163.24) * mm, "end": v(77.24, -118.32) * mm, "construction": true});
            skLineSegment(sketch, "E184.1.1.24", {"start": v(32.32, -163.24) * mm, "end": v(185.68, -226.76) * mm, "construction": true});
            skLineSegment(sketch, "E184.1.1.25", {"start": v(32.32, -226.76) * mm, "end": v(32.32, -163.24) * mm, "construction": true});
            skLineSegment(sketch, "E184.1.1.26", {"start": v(136.72, -268.44) * mm, "end": v(109.4, -202.49) * mm});
            skLineSegment(sketch, "E184.1.1.27", {"start": v(140.76, -271.68) * mm, "end": v(77.24, -271.68) * mm, "construction": true});
            skPoint(sketch, "E184.1.1.28", {"position": v(109, -195) * mm});
            skLineSegment(sketch, "E184.1.1.29", {"start": v(77.24, -118.32) * mm, "end": v(140.76, -271.68) * mm, "construction": true});
            skLineSegment(sketch, "E184.1.1.30", {"start": v(140.76, -118.32) * mm, "end": v(77.24, -271.68) * mm, "construction": true});
            skLineSegment(sketch, "E184.1.1.31", {"start": v(77.24, -271.68) * mm, "end": v(140.76, -118.32) * mm, "construction": true});
            skLineSegment(sketch, "E184.1.1.32", {"start": v(185.68, -226.76) * mm, "end": v(32.32, -163.24) * mm, "construction": true});
            skPoint(sketch, "E184.1.1.33", {"position": v(109, -195) * mm});
            skLineSegment(sketch, "E184.1.1.34", {"start": v(140.76, -271.68) * mm, "end": v(77.24, -118.32) * mm, "construction": true});
            skLineSegment(sketch, "E184.1.1.35", {"start": v(185.68, -163.24) * mm, "end": v(32.32, -226.76) * mm, "construction": true});
            skPoint(sketch, "E184.1.1.36", {"position": v(109, -195) * mm});
            skCircle(sketch, "E184.1.1.37", {"center": v(109, -195) * mm, "radius": 7.5 * mm});
            skCircle(sketch, "E184.1.1.38", {"center": v(32.32, -163.24) * mm, "radius": 1.25 * mm});
            skArc(sketch, "E184.1.1.39", {"start": v(37.47, -227.34) * mm, "mid": v(36.48, -225.04) * mm, "end": v(35.56, -222.72) * mm});
            skCircle(sketch, "E184.1.1.40", {"center": v(185.68, -163.24) * mm, "radius": 1.25 * mm});
            skCircle(sketch, "E184.1.1.41", {"center": v(32.32, -226.76) * mm, "radius": 1.25 * mm});
            skArc(sketch, "E184.1.1.42", {"start": v(136.72, -121.56) * mm, "mid": v(139.04, -122.48) * mm, "end": v(141.34, -123.47) * mm});
            skArc(sketch, "E184.1.1.43", {"start": v(76.66, -123.47) * mm, "mid": v(78.96, -122.48) * mm, "end": v(81.28, -121.56) * mm});
            skArc(sketch, "E184.1.1.44", {"start": v(81.28, -268.44) * mm, "mid": v(78.96, -267.52) * mm, "end": v(76.66, -266.53) * mm});
            skArc(sketch, "E184.1.1.45", {"start": v(180.53, -162.66) * mm, "mid": v(181.52, -164.96) * mm, "end": v(182.44, -167.28) * mm});
            skArc(sketch, "E184.1.1.46", {"start": v(35.56, -167.28) * mm, "mid": v(36.48, -164.96) * mm, "end": v(37.47, -162.66) * mm});
            skCircle(sketch, "E184.1.1.47", {"center": v(77.24, -118.32) * mm, "radius": 1.25 * mm});
            skCircle(sketch, "E184.1.1.48", {"center": v(140.76, -118.32) * mm, "radius": 1.25 * mm});
            skCircle(sketch, "E184.1.1.49", {"center": v(185.68, -226.76) * mm, "radius": 1.25 * mm});
            skArc(sketch, "E184.1.1.50", {"start": v(182.44, -222.72) * mm, "mid": v(181.52, -225.04) * mm, "end": v(180.53, -227.34) * mm});
            skCircle(sketch, "E184.1.1.51", {"center": v(77.24, -271.68) * mm, "radius": 1.25 * mm});
            skCircle(sketch, "E184.1.1.52", {"center": v(140.76, -271.68) * mm, "radius": 1.25 * mm});
            skArc(sketch, "E184.1.1.53", {"start": v(141.34, -266.53) * mm, "mid": v(139.04, -267.52) * mm, "end": v(136.72, -268.44) * mm});
            skCircle(sketch, "E184.1.1.54", {"center": v(109, -195) * mm, "radius": 2.5 * mm});
            skLineSegment(sketch, "E184.direction1", {"start": v(-140.76, -97.68) * mm, "end": v(77.24, -97.68) * mm, "construction": true});
            skLineSegment(sketch, "E184.direction2", {"start": v(-140.76, -97.68) * mm, "end": v(-140.76, -271.68) * mm, "construction": true});
            skSolve(sketch);
        }
        {
            var Q0;
            Q0 = qSketchRegion(id + "F10", true);
            extrude(context, id + "F11", {"entities" : qUnion([Q0]), "operationType" : NewBodyOperationType.ADD, "oppositeDirection" : true, "depth" : 2 * mm, "offsetDistance" : 25 * mm});
        }
        {
            var Q0;
            Q0=makeQuery(id+"F10.imprint","IMPRINT",FACE,{"disambiguationData":[TD([[makeQuery(id+"F10.imprint","IMPRINT",EDGE,{"derivedFrom":sQuery(id+"F10.wireOp",EDGE,"E173")}),1.0]])]});
            var Q1;
            Q1=makeQuery(id+"F10.imprint","IMPRINT",FACE,{"disambiguationData":[TD([[makeQuery(id+"F10.imprint","IMPRINT",EDGE,{"derivedFrom":sQuery(id+"F10.wireOp",EDGE,"E174.7.0")}),1.0]])]});
            var Q2;
            Q2=makeQuery(id+"F10.imprint","IMPRINT",FACE,{"disambiguationData":[TD([[makeQuery(id+"F10.imprint","IMPRINT",EDGE,{"derivedFrom":sQuery(id+"F10.wireOp",EDGE,"E174.6.0")}),1.0]])]});
            var Q3;
            Q3=makeQuery(id+"F10.imprint","IMPRINT",FACE,{"disambiguationData":[TD([[makeQuery(id+"F10.imprint","IMPRINT",EDGE,{"derivedFrom":sQuery(id+"F10.wireOp",EDGE,"E174.5.0")}),1.0]])]});
            var Q4;
            Q4=makeQuery(id+"F10.imprint","IMPRINT",FACE,{"disambiguationData":[TD([[makeQuery(id+"F10.imprint","IMPRINT",EDGE,{"derivedFrom":sQuery(id+"F10.wireOp",EDGE,"E174.4.0")}),1.0]])]});
            var Q5;
            Q5=makeQuery(id+"F10.imprint","IMPRINT",FACE,{"disambiguationData":[TD([[makeQuery(id+"F10.imprint","IMPRINT",EDGE,{"derivedFrom":sQuery(id+"F10.wireOp",EDGE,"E174.3.0")}),1.0]])]});
            var Q6;
            Q6=makeQuery(id+"F10.imprint","IMPRINT",FACE,{"disambiguationData":[TD([[makeQuery(id+"F10.imprint","IMPRINT",EDGE,{"derivedFrom":sQuery(id+"F10.wireOp",EDGE,"E174.2.0")}),1.0]])]});
            var Q7;
            Q7=makeQuery(id+"F10.imprint","IMPRINT",FACE,{"disambiguationData":[TD([[makeQuery(id+"F10.imprint","IMPRINT",EDGE,{"derivedFrom":sQuery(id+"F10.wireOp",EDGE,"E174.1.0")}),1.0]])]});
            var Q8;
            Q8=makeQuery(id+"F10.imprint","IMPRINT",FACE,{"disambiguationData":[TD([[makeQuery(id+"F10.imprint","IMPRINT",EDGE,{"derivedFrom":sQuery(id+"F10.wireOp",EDGE,"E184.1.0.47")}),1.0]])]});
            var Q9;
            Q9=makeQuery(id+"F10.imprint","IMPRINT",FACE,{"disambiguationData":[TD([[makeQuery(id+"F10.imprint","IMPRINT",EDGE,{"derivedFrom":sQuery(id+"F10.wireOp",EDGE,"E184.1.0.48")}),1.0]])]});
            var Q10;
            Q10=makeQuery(id+"F10.imprint","IMPRINT",FACE,{"disambiguationData":[TD([[makeQuery(id+"F10.imprint","IMPRINT",EDGE,{"derivedFrom":sQuery(id+"F10.wireOp",EDGE,"E184.1.0.38")}),1.0]])]});
            var Q11;
            Q11=makeQuery(id+"F10.imprint","IMPRINT",FACE,{"disambiguationData":[TD([[makeQuery(id+"F10.imprint","IMPRINT",EDGE,{"derivedFrom":sQuery(id+"F10.wireOp",EDGE,"E184.1.0.40")}),1.0]])]});
            var Q12;
            Q12=makeQuery(id+"F10.imprint","IMPRINT",FACE,{"disambiguationData":[TD([[makeQuery(id+"F10.imprint","IMPRINT",EDGE,{"derivedFrom":sQuery(id+"F10.wireOp",EDGE,"E184.1.0.52")}),1.0]])]});
            var Q13;
            Q13=makeQuery(id+"F10.imprint","IMPRINT",FACE,{"disambiguationData":[TD([[makeQuery(id+"F10.imprint","IMPRINT",EDGE,{"derivedFrom":sQuery(id+"F10.wireOp",EDGE,"E184.1.0.49")}),1.0]])]});
            var Q14;
            Q14=makeQuery(id+"F10.imprint","IMPRINT",FACE,{"disambiguationData":[TD([[makeQuery(id+"F10.imprint","IMPRINT",EDGE,{"derivedFrom":sQuery(id+"F10.wireOp",EDGE,"E184.1.0.51")}),1.0]])]});
            var Q15;
            Q15=makeQuery(id+"F10.imprint","IMPRINT",FACE,{"disambiguationData":[TD([[makeQuery(id+"F10.imprint","IMPRINT",EDGE,{"derivedFrom":sQuery(id+"F10.wireOp",EDGE,"E184.1.0.41")}),1.0]])]});
            var Q16;
            Q16=makeQuery(id+"F10.imprint","IMPRINT",FACE,{"disambiguationData":[TD([[makeQuery(id+"F10.imprint","IMPRINT",EDGE,{"derivedFrom":sQuery(id+"F10.wireOp",EDGE,"E184.1.1.47")}),1.0]])]});
            var Q17;
            Q17=makeQuery(id+"F10.imprint","IMPRINT",FACE,{"disambiguationData":[TD([[makeQuery(id+"F10.imprint","IMPRINT",EDGE,{"derivedFrom":sQuery(id+"F10.wireOp",EDGE,"E184.1.1.48")}),1.0]])]});
            var Q18;
            Q18=makeQuery(id+"F10.imprint","IMPRINT",FACE,{"disambiguationData":[TD([[makeQuery(id+"F10.imprint","IMPRINT",EDGE,{"derivedFrom":sQuery(id+"F10.wireOp",EDGE,"E184.1.1.40")}),1.0]])]});
            var Q19;
            Q19=makeQuery(id+"F10.imprint","IMPRINT",FACE,{"disambiguationData":[TD([[makeQuery(id+"F10.imprint","IMPRINT",EDGE,{"derivedFrom":sQuery(id+"F10.wireOp",EDGE,"E184.1.1.38")}),1.0]])]});
            var Q20;
            Q20=makeQuery(id+"F10.imprint","IMPRINT",FACE,{"disambiguationData":[TD([[makeQuery(id+"F10.imprint","IMPRINT",EDGE,{"derivedFrom":sQuery(id+"F10.wireOp",EDGE,"E184.1.1.49")}),1.0]])]});
            var Q21;
            Q21=makeQuery(id+"F10.imprint","IMPRINT",FACE,{"disambiguationData":[TD([[makeQuery(id+"F10.imprint","IMPRINT",EDGE,{"derivedFrom":sQuery(id+"F10.wireOp",EDGE,"E184.1.1.52")}),1.0]])]});
            var Q22;
            Q22=makeQuery(id+"F10.imprint","IMPRINT",FACE,{"disambiguationData":[TD([[makeQuery(id+"F10.imprint","IMPRINT",EDGE,{"derivedFrom":sQuery(id+"F10.wireOp",EDGE,"E184.1.1.51")}),1.0]])]});
            var Q23;
            Q23=makeQuery(id+"F10.imprint","IMPRINT",FACE,{"disambiguationData":[TD([[makeQuery(id+"F10.imprint","IMPRINT",EDGE,{"derivedFrom":sQuery(id+"F10.wireOp",EDGE,"E184.1.1.41")}),1.0]])]});
            var Q24;
            Q24=makeQuery(id+"F10.imprint","IMPRINT",FACE,{"disambiguationData":[TD([[makeQuery(id+"F10.imprint","IMPRINT",EDGE,{"derivedFrom":sQuery(id+"F10.wireOp",EDGE,"E184.0.1.52")}),1.0]])]});
            var Q25;
            Q25=makeQuery(id+"F10.imprint","IMPRINT",FACE,{"disambiguationData":[TD([[makeQuery(id+"F10.imprint","IMPRINT",EDGE,{"derivedFrom":sQuery(id+"F10.wireOp",EDGE,"E184.0.1.49")}),1.0]])]});
            var Q26;
            Q26=makeQuery(id+"F10.imprint","IMPRINT",FACE,{"disambiguationData":[TD([[makeQuery(id+"F10.imprint","IMPRINT",EDGE,{"derivedFrom":sQuery(id+"F10.wireOp",EDGE,"E184.0.1.40")}),1.0]])]});
            var Q27;
            Q27=makeQuery(id+"F10.imprint","IMPRINT",FACE,{"disambiguationData":[TD([[makeQuery(id+"F10.imprint","IMPRINT",EDGE,{"derivedFrom":sQuery(id+"F10.wireOp",EDGE,"E184.0.1.48")}),1.0]])]});
            var Q28;
            Q28=makeQuery(id+"F10.imprint","IMPRINT",FACE,{"disambiguationData":[TD([[makeQuery(id+"F10.imprint","IMPRINT",EDGE,{"derivedFrom":sQuery(id+"F10.wireOp",EDGE,"E184.0.1.47")}),1.0]])]});
            var Q29;
            Q29=makeQuery(id+"F10.imprint","IMPRINT",FACE,{"disambiguationData":[TD([[makeQuery(id+"F10.imprint","IMPRINT",EDGE,{"derivedFrom":sQuery(id+"F10.wireOp",EDGE,"E184.0.1.38")}),1.0]])]});
            var Q30;
            Q30=makeQuery(id+"F10.imprint","IMPRINT",FACE,{"disambiguationData":[TD([[makeQuery(id+"F10.imprint","IMPRINT",EDGE,{"derivedFrom":sQuery(id+"F10.wireOp",EDGE,"E184.0.1.41")}),1.0]])]});
            var Q31;
            Q31=makeQuery(id+"F10.imprint","IMPRINT",FACE,{"disambiguationData":[TD([[makeQuery(id+"F10.imprint","IMPRINT",EDGE,{"derivedFrom":sQuery(id+"F10.wireOp",EDGE,"E184.0.1.51")}),1.0]])]});
            extrude(context, id + "F12", {"entities" : qUnion([Q0, Q1, Q2, Q3, Q4, Q5, Q6, Q7, Q8, Q9, Q10, Q11, Q12, Q13, Q14, Q15, Q16, Q17, Q18, Q19, Q20, Q21, Q22, Q23, Q24, Q25, Q26, Q27, Q28, Q29, Q30, Q31]), "operationType" : NewBodyOperationType.REMOVE, "endBound" : BoundingType.THROUGH_ALL, "oppositeDirection" : true, "depth" : 25 * mm, "offsetDistance" : 25 * mm});
        }
        {
            var Q0;
            Q0 = qSketchRegion(id + "F9", true);
            var Q1;
            Q1=makeQuery(id+"F9.imprint","IMPRINT",FACE,{"disambiguationData":[TD([[makeQuery(id+"F9.imprint","IMPRINT",EDGE,{"derivedFrom":sQuery(id+"F9.wireOp",EDGE,"E146")}),1.0]])]});
            extrude(context, id + "F13", {"entities" : qUnion([Q0, Q1]), "operationType" : NewBodyOperationType.ADD, "oppositeDirection" : true, "depth" : 2 * mm, "offsetDistance" : 25 * mm});
        }
    });
